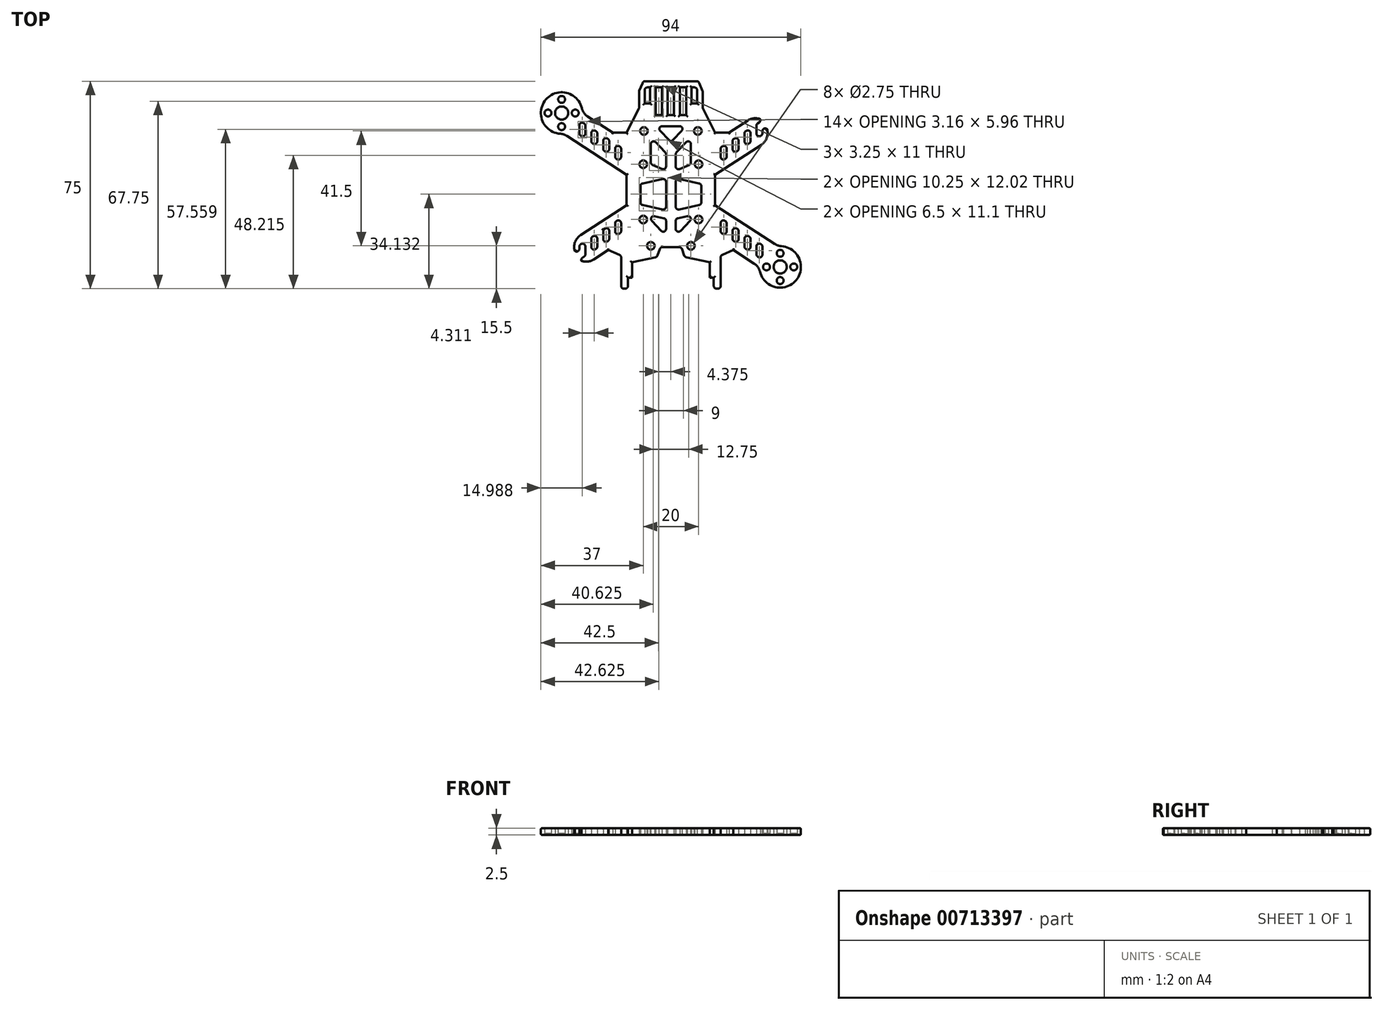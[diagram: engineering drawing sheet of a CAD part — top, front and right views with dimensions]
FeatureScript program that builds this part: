
annotation { "Feature Type Name" : "Feature", "Feature Type Description" : "" }
export const myFeature = defineFeature(function(context is Context, id is Id, definition is map)
    precondition{}
    {
        {
            assignVariable(context, id + "F0", {"name" : "PlateThickness", "anyValue" : 2.5});
        }
        {
            var Q0;
            Q0=qCreatedBy(makeId("Top.planeOp"),FACE);
            var sketch = newSketch(context, id + "F1", { "sketchPlane" : qUnion([Q0])});
            skLineSegment(sketch, "E0.bottom", {"start": v(-10, 35) * mm, "end": v(10, 35) * mm});
            skLineSegment(sketch, "E0.top", {"start": v(-16, -25) * mm, "end": v(16, -25) * mm});
            skLineSegment(sketch, "E0.left", {"start": v(-16, 16.36) * mm, "end": v(-16, -25) * mm});
            skLineSegment(sketch, "E0.right", {"start": v(16, 16.36) * mm, "end": v(16, -25) * mm});
            skPoint(sketch, "E0.middle", {"position": v(0, 5) * mm});
            skLineSegment(sketch, "E1", {"start": v(-10, 35) * mm, "end": v(-11.5, 31.3) * mm});
            skLineSegment(sketch, "E2", {"start": v(-11.5, 31.3) * mm, "end": v(-11.5, 25.3) * mm});
            skLineSegment(sketch, "E3", {"start": v(-11.5, 25.3) * mm, "end": v(-16, 16.36) * mm});
            skPoint(sketch, "E4.orphan", {"position": v(-16, 35) * mm});
            skLineSegment(sketch, "E5", {"start": v(-16, 16.36) * mm, "end": v(-21, 16.36) * mm});
            skLineSegment(sketch, "E6", {"start": v(-21, 16.36) * mm, "end": v(-32, 23.52) * mm});
            skLineSegment(sketch, "E7", {"start": v(-38.83, 16.03) * mm, "end": v(-16, 1.18) * mm});
            skCircle(sketch, "E8", {"center": v(-39.5, 23.5) * mm, "radius": 7.5 * mm});
            skLineSegment(sketch, "E9", {"start": v(0, -4.32) * mm, "end": v(-32.42, -4.32) * mm, "construction": true});
            skLineSegment(sketch, "E10.MirrorCS", {"start": v(-38.83, -24.67) * mm, "end": v(-16, -9.82) * mm});
            skCircle(sketch, "E11.MirrorC", {"center": v(-39.5, -32.14) * mm, "radius": 7.5 * mm});
            skLineSegment(sketch, "E12.MirrorCS", {"start": v(-21, -25) * mm, "end": v(-32, -32.15) * mm});
            skLineSegment(sketch, "E13.MirrorCS", {"start": v(-16, -25) * mm, "end": v(-21, -25) * mm});
            skLineSegment(sketch, "E14.MirrorCS", {"start": v(38.83, 16.03) * mm, "end": v(16, 1.18) * mm});
            skLineSegment(sketch, "E15.MirrorCS", {"start": v(21, 16.36) * mm, "end": v(32, 23.52) * mm});
            skLineSegment(sketch, "E16.MirrorCS", {"start": v(16, 16.36) * mm, "end": v(21, 16.36) * mm});
            skCircle(sketch, "E17.MirrorC", {"center": v(39.5, 23.5) * mm, "radius": 7.5 * mm});
            skLineSegment(sketch, "E18.MirrorCS", {"start": v(38.83, -24.67) * mm, "end": v(16, -9.82) * mm});
            skLineSegment(sketch, "E19.MirrorCS", {"start": v(21, -25) * mm, "end": v(32, -32.15) * mm});
            skLineSegment(sketch, "E20.MirrorCS", {"start": v(16, -25) * mm, "end": v(21, -25) * mm});
            skCircle(sketch, "E21.MirrorC", {"center": v(39.5, -32.14) * mm, "radius": 7.5 * mm});
            skLineSegment(sketch, "E22.MirrorCS", {"start": v(10, 35) * mm, "end": v(11.5, 31.3) * mm});
            skLineSegment(sketch, "E23.MirrorCS", {"start": v(11.5, 31.3) * mm, "end": v(11.5, 25.3) * mm});
            skLineSegment(sketch, "E24.MirrorCS", {"start": v(11.5, 25.3) * mm, "end": v(16, 16.36) * mm});
            skPoint(sketch, "E25.orphan", {"position": v(16, 35) * mm});
            skCircle(sketch, "E26", {"center": v(-39.5, 23.5) * mm, "radius": 2.38 * mm});
            skCircle(sketch, "E27", {"center": v(-39.5, 28.42) * mm, "radius": 1.25 * mm});
            skLineSegment(sketch, "E28", {"start": v(-39.5, 23.5) * mm, "end": v(-47, 23.5) * mm, "construction": true});
            skCircle(sketch, "E29.MirrorC", {"center": v(-39.5, 18.58) * mm, "radius": 1.25 * mm});
            skCircle(sketch, "E30", {"center": v(-44.42, 23.5) * mm, "radius": 1.25 * mm});
            skLineSegment(sketch, "E31", {"start": v(-39.5, 23.5) * mm, "end": v(-39.5, 31) * mm, "construction": true});
            skCircle(sketch, "E32.MirrorC", {"center": v(-34.58, 23.5) * mm, "radius": 1.25 * mm});
            skLineSegment(sketch, "E33", {"start": v(-33.09, 15.63) * mm, "end": v(-18, 5.82) * mm});
            skLineSegment(sketch, "E34", {"start": v(-18, 5.82) * mm, "end": v(-18, 11.07) * mm});
            skLineSegment(sketch, "E35", {"start": v(-18, 11.07) * mm, "end": v(-33.09, 20.88) * mm});
            skLineSegment(sketch, "E36", {"start": v(-33.09, 20.88) * mm, "end": v(-33.09, 15.63) * mm});
            skLineSegment(sketch, "E37", {"start": v(-25.54, 15.98) * mm, "end": v(-25.54, 19.32) * mm, "construction": true});
            skLineSegment(sketch, "E38", {"start": v(-25.54, 10.73) * mm, "end": v(-25.54, 7.39) * mm, "construction": true});
            skLineSegment(sketch, "E39", {"start": v(-30.93, 19.48) * mm, "end": v(-30.93, 14.23) * mm});
            skLineSegment(sketch, "E40", {"start": v(-28.78, 18.08) * mm, "end": v(-28.78, 12.83) * mm});
            skLineSegment(sketch, "E41", {"start": v(-26.62, 16.68) * mm, "end": v(-26.62, 11.43) * mm});
            skLineSegment(sketch, "E42", {"start": v(-24.47, 15.28) * mm, "end": v(-24.47, 10.03) * mm});
            skLineSegment(sketch, "E43", {"start": v(-22.31, 13.87) * mm, "end": v(-22.31, 8.62) * mm});
            skLineSegment(sketch, "E44", {"start": v(-20.16, 12.47) * mm, "end": v(-20.16, 7.22) * mm});
            skLineSegment(sketch, "E45", {"start": v(-33.09, 15.63) * mm, "end": v(-30.93, 14.23) * mm, "construction": true});
            skLineSegment(sketch, "E46", {"start": v(-30.93, 14.23) * mm, "end": v(-28.78, 12.83) * mm, "construction": true});
            skLineSegment(sketch, "E47", {"start": v(-28.78, 12.83) * mm, "end": v(-26.62, 11.43) * mm, "construction": true});
            skLineSegment(sketch, "E48", {"start": v(-26.62, 11.43) * mm, "end": v(-24.47, 10.03) * mm, "construction": true});
            skLineSegment(sketch, "E49", {"start": v(-24.47, 10.03) * mm, "end": v(-22.31, 8.62) * mm, "construction": true});
            skLineSegment(sketch, "E50", {"start": v(-22.31, 8.62) * mm, "end": v(-20.16, 7.22) * mm, "construction": true});
            skLineSegment(sketch, "E51", {"start": v(-20.16, 7.22) * mm, "end": v(-18, 5.82) * mm, "construction": true});
            skLineSegment(sketch, "E52.MirrorCS", {"start": v(33.09, 15.63) * mm, "end": v(18, 5.82) * mm});
            skLineSegment(sketch, "E53.MirrorCS", {"start": v(26.62, 11.43) * mm, "end": v(24.47, 10.03) * mm, "construction": true});
            skLineSegment(sketch, "E54.MirrorCS", {"start": v(30.93, 14.23) * mm, "end": v(28.78, 12.83) * mm, "construction": true});
            skLineSegment(sketch, "E55.MirrorCS", {"start": v(25.54, 15.98) * mm, "end": v(25.54, 19.32) * mm, "construction": true});
            skLineSegment(sketch, "E56.MirrorCS", {"start": v(33.09, 15.63) * mm, "end": v(30.93, 14.23) * mm, "construction": true});
            skLineSegment(sketch, "E57.MirrorCS", {"start": v(22.31, 8.62) * mm, "end": v(20.16, 7.22) * mm, "construction": true});
            skLineSegment(sketch, "E58.MirrorCS", {"start": v(28.78, 18.08) * mm, "end": v(28.78, 12.83) * mm});
            skLineSegment(sketch, "E59.MirrorCS", {"start": v(30.93, 19.48) * mm, "end": v(30.93, 14.23) * mm});
            skLineSegment(sketch, "E60.MirrorCS", {"start": v(24.47, 15.28) * mm, "end": v(24.47, 10.03) * mm});
            skLineSegment(sketch, "E61.MirrorCS", {"start": v(18, 11.07) * mm, "end": v(33.09, 20.88) * mm});
            skLineSegment(sketch, "E62.MirrorCS", {"start": v(24.47, 10.03) * mm, "end": v(22.31, 8.62) * mm, "construction": true});
            skLineSegment(sketch, "E63.MirrorCS", {"start": v(28.78, 12.83) * mm, "end": v(26.62, 11.43) * mm, "construction": true});
            skLineSegment(sketch, "E64.MirrorCS", {"start": v(26.62, 16.68) * mm, "end": v(26.62, 11.43) * mm});
            skLineSegment(sketch, "E65.MirrorCS", {"start": v(20.16, 12.47) * mm, "end": v(20.16, 7.22) * mm});
            skLineSegment(sketch, "E66.MirrorCS", {"start": v(33.09, 20.88) * mm, "end": v(33.09, 15.63) * mm});
            skLineSegment(sketch, "E67.MirrorCS", {"start": v(25.54, 10.73) * mm, "end": v(25.54, 7.39) * mm, "construction": true});
            skLineSegment(sketch, "E68.MirrorCS", {"start": v(18, 5.82) * mm, "end": v(18, 11.07) * mm});
            skLineSegment(sketch, "E69.MirrorCS", {"start": v(20.16, 7.22) * mm, "end": v(18, 5.82) * mm, "construction": true});
            skLineSegment(sketch, "E70.MirrorCS", {"start": v(22.31, 13.87) * mm, "end": v(22.31, 8.62) * mm});
            skCircle(sketch, "E71.MirrorC", {"center": v(39.5, 18.58) * mm, "radius": 1.25 * mm});
            skCircle(sketch, "E72.MirrorC", {"center": v(34.58, 23.5) * mm, "radius": 1.25 * mm});
            skCircle(sketch, "E73.MirrorC", {"center": v(39.5, 23.5) * mm, "radius": 2.38 * mm});
            skCircle(sketch, "E74.MirrorC", {"center": v(39.5, 28.43) * mm, "radius": 1.25 * mm});
            skCircle(sketch, "E75.MirrorC", {"center": v(44.42, 23.5) * mm, "radius": 1.25 * mm});
            skLineSegment(sketch, "E76.MirrorCS", {"start": v(33.09, -24.27) * mm, "end": v(18, -14.46) * mm});
            skLineSegment(sketch, "E77.MirrorCS", {"start": v(30.93, -22.87) * mm, "end": v(28.78, -21.47) * mm, "construction": true});
            skLineSegment(sketch, "E78.MirrorCS", {"start": v(28.78, -21.47) * mm, "end": v(26.62, -20.07) * mm, "construction": true});
            skLineSegment(sketch, "E79.MirrorCS", {"start": v(24.47, -18.67) * mm, "end": v(22.31, -17.26) * mm, "construction": true});
            skLineSegment(sketch, "E80.MirrorCS", {"start": v(22.31, -17.26) * mm, "end": v(20.16, -15.86) * mm, "construction": true});
            skLineSegment(sketch, "E81.MirrorCS", {"start": v(20.16, -15.86) * mm, "end": v(18, -14.46) * mm, "construction": true});
            skLineSegment(sketch, "E82.MirrorCS", {"start": v(26.62, -20.07) * mm, "end": v(24.47, -18.67) * mm, "construction": true});
            skLineSegment(sketch, "E83.MirrorCS", {"start": v(33.09, -24.27) * mm, "end": v(30.93, -22.87) * mm, "construction": true});
            skLineSegment(sketch, "E84.MirrorCS", {"start": v(24.47, -23.92) * mm, "end": v(24.47, -18.67) * mm});
            skLineSegment(sketch, "E85.MirrorCS", {"start": v(18, -14.46) * mm, "end": v(18, -19.7) * mm});
            skLineSegment(sketch, "E86.MirrorCS", {"start": v(25.54, -19.37) * mm, "end": v(25.54, -16.03) * mm, "construction": true});
            skLineSegment(sketch, "E87.MirrorCS", {"start": v(22.31, -22.51) * mm, "end": v(22.31, -17.26) * mm});
            skLineSegment(sketch, "E88.MirrorCS", {"start": v(28.78, -26.72) * mm, "end": v(28.78, -21.47) * mm});
            skLineSegment(sketch, "E89.MirrorCS", {"start": v(30.93, -28.12) * mm, "end": v(30.93, -22.87) * mm});
            skLineSegment(sketch, "E90.MirrorCS", {"start": v(25.54, -24.62) * mm, "end": v(25.54, -27.96) * mm, "construction": true});
            skLineSegment(sketch, "E91.MirrorCS", {"start": v(26.62, -25.32) * mm, "end": v(26.62, -20.07) * mm});
            skLineSegment(sketch, "E92.MirrorCS", {"start": v(20.16, -21.11) * mm, "end": v(20.16, -15.86) * mm});
            skLineSegment(sketch, "E93.MirrorCS", {"start": v(18, -19.7) * mm, "end": v(33.09, -29.52) * mm});
            skLineSegment(sketch, "E94.MirrorCS", {"start": v(33.09, -29.52) * mm, "end": v(33.09, -24.27) * mm});
            skCircle(sketch, "E95.MirrorC", {"center": v(39.5, -27.21) * mm, "radius": 1.25 * mm});
            skCircle(sketch, "E96.MirrorC", {"center": v(39.5, -32.14) * mm, "radius": 2.38 * mm});
            skCircle(sketch, "E97.MirrorC", {"center": v(34.58, -32.14) * mm, "radius": 1.25 * mm});
            skCircle(sketch, "E98.MirrorC", {"center": v(39.5, -37.06) * mm, "radius": 1.25 * mm});
            skCircle(sketch, "E99.MirrorC", {"center": v(44.42, -32.14) * mm, "radius": 1.25 * mm});
            skLineSegment(sketch, "E100.MirrorCS", {"start": v(-28.78, -21.47) * mm, "end": v(-26.62, -20.07) * mm, "construction": true});
            skLineSegment(sketch, "E101.MirrorCS", {"start": v(-33.09, -24.27) * mm, "end": v(-18, -14.46) * mm});
            skLineSegment(sketch, "E102.MirrorCS", {"start": v(-26.62, -20.07) * mm, "end": v(-24.47, -18.67) * mm, "construction": true});
            skLineSegment(sketch, "E103.MirrorCS", {"start": v(-25.54, -19.37) * mm, "end": v(-25.54, -16.03) * mm, "construction": true});
            skLineSegment(sketch, "E104.MirrorCS", {"start": v(-26.62, -25.32) * mm, "end": v(-26.62, -20.07) * mm});
            skLineSegment(sketch, "E105.MirrorCS", {"start": v(-24.47, -23.92) * mm, "end": v(-24.47, -18.67) * mm});
            skLineSegment(sketch, "E106.MirrorCS", {"start": v(-24.47, -18.67) * mm, "end": v(-22.31, -17.26) * mm, "construction": true});
            skLineSegment(sketch, "E107.MirrorCS", {"start": v(-28.78, -26.72) * mm, "end": v(-28.78, -21.47) * mm});
            skLineSegment(sketch, "E108.MirrorCS", {"start": v(-33.09, -24.27) * mm, "end": v(-30.93, -22.87) * mm, "construction": true});
            skLineSegment(sketch, "E109.MirrorCS", {"start": v(-22.31, -17.26) * mm, "end": v(-20.16, -15.86) * mm, "construction": true});
            skLineSegment(sketch, "E110.MirrorCS", {"start": v(-22.31, -22.51) * mm, "end": v(-22.31, -17.26) * mm});
            skLineSegment(sketch, "E111.MirrorCS", {"start": v(-30.93, -22.87) * mm, "end": v(-28.78, -21.47) * mm, "construction": true});
            skLineSegment(sketch, "E112.MirrorCS", {"start": v(-20.16, -15.86) * mm, "end": v(-18, -14.46) * mm, "construction": true});
            skLineSegment(sketch, "E113.MirrorCS", {"start": v(-20.16, -21.11) * mm, "end": v(-20.16, -15.86) * mm});
            skLineSegment(sketch, "E114.MirrorCS", {"start": v(-33.09, -29.52) * mm, "end": v(-33.09, -24.27) * mm});
            skLineSegment(sketch, "E115.MirrorCS", {"start": v(-25.54, -24.62) * mm, "end": v(-25.54, -27.96) * mm, "construction": true});
            skLineSegment(sketch, "E116.MirrorCS", {"start": v(-18, -14.46) * mm, "end": v(-18, -19.7) * mm});
            skLineSegment(sketch, "E117.MirrorCS", {"start": v(-30.93, -28.12) * mm, "end": v(-30.93, -22.87) * mm});
            skLineSegment(sketch, "E118.MirrorCS", {"start": v(-18, -19.7) * mm, "end": v(-33.09, -29.52) * mm});
            skCircle(sketch, "E119.MirrorC", {"center": v(-39.5, -27.21) * mm, "radius": 1.25 * mm});
            skCircle(sketch, "E120.MirrorC", {"center": v(-34.58, -32.14) * mm, "radius": 1.25 * mm});
            skCircle(sketch, "E121.MirrorC", {"center": v(-44.42, -32.14) * mm, "radius": 1.25 * mm});
            skCircle(sketch, "E122.MirrorC", {"center": v(-39.5, -37.06) * mm, "radius": 1.25 * mm});
            skCircle(sketch, "E123.MirrorC", {"center": v(-39.5, -32.14) * mm, "radius": 2.38 * mm});
            skLineSegment(sketch, "E124.bottom", {"start": v(-7.5, 27) * mm, "end": v(-9.5, 27) * mm});
            skLineSegment(sketch, "E124.top", {"start": v(-7.5, 32.75) * mm, "end": v(-9.5, 32.75) * mm});
            skLineSegment(sketch, "E124.left", {"start": v(-7.5, 27) * mm, "end": v(-7.5, 32.75) * mm});
            skLineSegment(sketch, "E124.right", {"start": v(-9.5, 27) * mm, "end": v(-9.5, 32.75) * mm});
            skPoint(sketch, "E124.middle", {"position": v(-8.5, 29.88) * mm});
            skLineSegment(sketch, "E125.MirrorCS", {"start": v(7.5, 27) * mm, "end": v(9.5, 27) * mm});
            skLineSegment(sketch, "E126.MirrorCS", {"start": v(7.5, 27) * mm, "end": v(7.5, 32.75) * mm});
            skLineSegment(sketch, "E127.MirrorCS", {"start": v(9.5, 27) * mm, "end": v(9.5, 32.75) * mm});
            skLineSegment(sketch, "E128.MirrorCS", {"start": v(7.5, 32.75) * mm, "end": v(9.5, 32.75) * mm});
            skLineSegment(sketch, "E129.bottom", {"start": v(-5.5, 32.75) * mm, "end": v(-3.25, 32.75) * mm});
            skLineSegment(sketch, "E129.top", {"start": v(-5.5, 22.75) * mm, "end": v(-3.25, 22.75) * mm});
            skLineSegment(sketch, "E129.left", {"start": v(-5.5, 32.75) * mm, "end": v(-5.5, 22.75) * mm});
            skLineSegment(sketch, "E129.right", {"start": v(-3.25, 32.75) * mm, "end": v(-3.25, 22.75) * mm});
            skPoint(sketch, "E129.middle", {"position": v(-4.37, 27.75) * mm});
            skLineSegment(sketch, "E130.MirrorCS", {"start": v(3.25, 32.75) * mm, "end": v(3.25, 22.75) * mm});
            skLineSegment(sketch, "E131.MirrorCS", {"start": v(5.5, 32.75) * mm, "end": v(3.25, 32.75) * mm});
            skLineSegment(sketch, "E132.MirrorCS", {"start": v(5.5, 32.75) * mm, "end": v(5.5, 22.75) * mm});
            skLineSegment(sketch, "E133.MirrorCS", {"start": v(5.5, 22.75) * mm, "end": v(3.25, 22.75) * mm});
            skLineSegment(sketch, "E134.bottom", {"start": v(-1.13, 32.75) * mm, "end": v(1.12, 32.75) * mm});
            skLineSegment(sketch, "E134.top", {"start": v(-1.13, 22.75) * mm, "end": v(1.12, 22.75) * mm});
            skLineSegment(sketch, "E134.left", {"start": v(-1.13, 32.75) * mm, "end": v(-1.13, 22.75) * mm});
            skLineSegment(sketch, "E134.right", {"start": v(1.12, 32.75) * mm, "end": v(1.13, 22.75) * mm});
            skPoint(sketch, "E134.middle", {"position": v(0, 27.75) * mm});
            skLineSegment(sketch, "E135", {"start": v(-5.5, 18.75) * mm, "end": v(5.5, 18.75) * mm});
            skLineSegment(sketch, "E136", {"start": v(5.5, 18.75) * mm, "end": v(0, 12.94) * mm});
            skLineSegment(sketch, "E137", {"start": v(0, 12.94) * mm, "end": v(-5.5, 18.75) * mm});
            skLineSegment(sketch, "E138", {"start": v(-7.25, 14.78) * mm, "end": v(-1.75, 8.97) * mm});
            skLineSegment(sketch, "E139", {"start": v(-1.75, 8.97) * mm, "end": v(-1.75, 2.63) * mm});
            skLineSegment(sketch, "E140", {"start": v(-1.75, 2.63) * mm, "end": v(-7.25, 5.03) * mm});
            skLineSegment(sketch, "E141", {"start": v(-7.25, 5.03) * mm, "end": v(-7.25, 14.78) * mm});
            skLineSegment(sketch, "E142.MirrorCS", {"start": v(1.75, 8.97) * mm, "end": v(1.75, 2.63) * mm});
            skLineSegment(sketch, "E143.MirrorCS", {"start": v(7.25, 14.78) * mm, "end": v(1.75, 8.97) * mm});
            skLineSegment(sketch, "E144.MirrorCS", {"start": v(7.25, 5.03) * mm, "end": v(7.25, 14.78) * mm});
            skLineSegment(sketch, "E145.MirrorCS", {"start": v(1.75, 2.63) * mm, "end": v(7.25, 5.03) * mm});
            skLineSegment(sketch, "E146", {"start": v(-11, -2.12) * mm, "end": v(-11, -9.62) * mm});
            skLineSegment(sketch, "E147", {"start": v(-11, -9.62) * mm, "end": v(-1.75, -11.62) * mm});
            skLineSegment(sketch, "E148", {"start": v(-1.75, -11.62) * mm, "end": v(-1.75, -0.12) * mm});
            skLineSegment(sketch, "E149", {"start": v(-1.75, -0.12) * mm, "end": v(-11, -2.12) * mm});
            skLineSegment(sketch, "E150.MirrorCS", {"start": v(1.75, -0.12) * mm, "end": v(11, -2.12) * mm});
            skLineSegment(sketch, "E151.MirrorCS", {"start": v(1.75, -11.62) * mm, "end": v(1.75, -0.12) * mm});
            skLineSegment(sketch, "E152.MirrorCS", {"start": v(11, -2.12) * mm, "end": v(11, -9.62) * mm});
            skLineSegment(sketch, "E153.MirrorCS", {"start": v(11, -9.62) * mm, "end": v(1.75, -11.62) * mm});
            skLineSegment(sketch, "E154", {"start": v(-9.1, -13.1) * mm, "end": v(-1.75, -14.69) * mm});
            skLineSegment(sketch, "E155", {"start": v(-1.75, -14.69) * mm, "end": v(-1.75, -20.94) * mm});
            skLineSegment(sketch, "E156", {"start": v(-1.75, -20.94) * mm, "end": v(-9.1, -13.1) * mm});
            skLineSegment(sketch, "E157.MirrorCS", {"start": v(9.1, -13.1) * mm, "end": v(1.75, -14.69) * mm});
            skLineSegment(sketch, "E158.MirrorCS", {"start": v(1.75, -14.69) * mm, "end": v(1.75, -20.94) * mm});
            skLineSegment(sketch, "E159.MirrorCS", {"start": v(1.75, -20.94) * mm, "end": v(9.1, -13.1) * mm});
            skLineSegment(sketch, "E160", {"start": v(-3.75, -25) * mm, "end": v(-5, -28.5) * mm});
            skLineSegment(sketch, "E161", {"start": v(-5, -28.5) * mm, "end": v(-14, -30.5) * mm});
            skLineSegment(sketch, "E162", {"start": v(-14, -30.5) * mm, "end": v(-14, -36) * mm});
            skLineSegment(sketch, "E163", {"start": v(-14, -36) * mm, "end": v(-15.5, -36) * mm});
            skLineSegment(sketch, "E164", {"start": v(-15.5, -36) * mm, "end": v(-15.5, -40) * mm});
            skLineSegment(sketch, "E165", {"start": v(-15.5, -40) * mm, "end": v(-18, -40) * mm});
            skLineSegment(sketch, "E166", {"start": v(-18, -40) * mm, "end": v(-18, -28) * mm});
            skLineSegment(sketch, "E167", {"start": v(-18, -28) * mm, "end": v(-22.6, -26.04) * mm});
            skLineSegment(sketch, "E168.MirrorCS", {"start": v(3.75, -25) * mm, "end": v(5, -28.5) * mm});
            skLineSegment(sketch, "E169.MirrorCS", {"start": v(5, -28.5) * mm, "end": v(14, -30.5) * mm});
            skLineSegment(sketch, "E170.MirrorCS", {"start": v(14, -30.5) * mm, "end": v(14, -36) * mm});
            skLineSegment(sketch, "E171.MirrorCS", {"start": v(15.5, -36) * mm, "end": v(15.5, -40) * mm});
            skLineSegment(sketch, "E172.MirrorCS", {"start": v(15.5, -40) * mm, "end": v(18, -40) * mm});
            skLineSegment(sketch, "E173.MirrorCS", {"start": v(18, -40) * mm, "end": v(18, -28) * mm});
            skLineSegment(sketch, "E174.MirrorCS", {"start": v(18, -28) * mm, "end": v(22.6, -26.04) * mm});
            skLineSegment(sketch, "E175.MirrorCS", {"start": v(14, -36) * mm, "end": v(15.5, -36) * mm});
            skCircle(sketch, "E176", {"center": v(-9.75, 17) * mm, "radius": 1.38 * mm});
            skCircle(sketch, "E177.MirrorC", {"center": v(9.75, 17) * mm, "radius": 1.38 * mm});
            skCircle(sketch, "E178", {"center": v(-7.25, -24.5) * mm, "radius": 1.38 * mm});
            skCircle(sketch, "E179.MirrorC", {"center": v(7.25, -24.5) * mm, "radius": 1.38 * mm});
            skCircle(sketch, "E180", {"center": v(10, 5) * mm, "radius": 1.38 * mm});
            skCircle(sketch, "E181", {"center": v(10, -15) * mm, "radius": 1.38 * mm});
            skCircle(sketch, "E182", {"center": v(-10, -15) * mm, "radius": 1.38 * mm});
            skCircle(sketch, "E183", {"center": v(-10, 5) * mm, "radius": 1.38 * mm});
            skPoint(sketch, "E184", {"position": v(-39.5, 0) * mm});
            skSolve(sketch);
        }
        {
            var Q0;
            Q0=makeQuery(id+"F1.imprint","IMPRINT",FACE,{"disambiguationData":[TD([[makeQuery(id+"F1.imprint","IMPRINT",EDGE,{"derivedFrom":sQuery(id+"F1.wireOp",EDGE,"E0.bottom")}),-1.0]])]});
            var Q1;
            {var subQ15=sQuery(id+"F1.wireOp",EDGE,"E5");Q1=makeQuery(id+"F1.imprint","IMPRINT",FACE,{"disambiguationData":[TD([[makeQuery(id+"F1.imprint","IMPRINT",EDGE,{"derivedFrom":subQ15}),1.0]])]});}
            var Q2;
            Q2=makeQuery(id+"F1.imprint","IMPRINT",FACE,{"disambiguationData":[TD([[makeQuery(id+"F1.imprint","IMPRINT",EDGE,{"derivedFrom":sQuery(id+"F1.wireOp",EDGE,"E26")}),-1.0]])]});
            var Q3;
            {var subQ2=sQuery(id+"F1.wireOp",EDGE,"E14.MirrorCS");Q3=makeQuery(id+"F1.imprint","IMPRINT",FACE,{"disambiguationData":[TD([[makeQuery(id+"F1.imprint","IMPRINT",EDGE,{"derivedFrom":subQ2}),-1.0]])]});}
            var Q4;
            {var subQ0=sQuery(id+"F1.wireOp",EDGE,"E17.MirrorC");var subQ1=makeQuery(id+"F1.imprint","INTERSECT",VERTEX,{"derivedFrom":[sQuery(id+"F1.wireOp",EDGE,"E14.MirrorCS"),subQ0]});Q4=makeQuery(id+"F1.imprint","IMPRINT",FACE,{"disambiguationData":[TD([[makeQuery(id+"F1.imprint","IMPRINT",EDGE,{"disambiguationData":[TD([[subQ1,1.0]])],"derivedFrom":subQ0}),-1.0]])]});}
            var Q5;
            {var subQ1=sQuery(id+"F1.wireOp",EDGE,"E18.MirrorCS");Q5=makeQuery(id+"F1.imprint","IMPRINT",FACE,{"disambiguationData":[TD([[makeQuery(id+"F1.imprint","IMPRINT",EDGE,{"derivedFrom":subQ1}),1.0]])]});}
            var Q6;
            {var subQ2=sQuery(id+"F1.wireOp",EDGE,"E10.MirrorCS");Q6=makeQuery(id+"F1.imprint","IMPRINT",FACE,{"disambiguationData":[TD([[makeQuery(id+"F1.imprint","IMPRINT",EDGE,{"derivedFrom":subQ2}),-1.0]])]});}
            var Q7;
            {var subQ0=sQuery(id+"F1.wireOp",EDGE,"E21.MirrorC");var subQ1=makeQuery(id+"F1.imprint","INTERSECT",VERTEX,{"derivedFrom":[sQuery(id+"F1.wireOp",EDGE,"E18.MirrorCS"),subQ0]});Q7=makeQuery(id+"F1.imprint","IMPRINT",FACE,{"disambiguationData":[TD([[makeQuery(id+"F1.imprint","IMPRINT",EDGE,{"disambiguationData":[TD([[subQ1,1.0]])],"derivedFrom":subQ0}),1.0]])]});}
            var Q8;
            {var subQ0=sQuery(id+"F1.wireOp",EDGE,"E39");Q8=makeQuery(id+"F1.imprint","IMPRINT",FACE,{"disambiguationData":[TD([[makeQuery(id+"F1.imprint","IMPRINT",EDGE,{"derivedFrom":subQ0}),1.0]])]});}
            var Q9;
            {var subQ0=sQuery(id+"F1.wireOp",EDGE,"E41");Q9=makeQuery(id+"F1.imprint","IMPRINT",FACE,{"disambiguationData":[TD([[makeQuery(id+"F1.imprint","IMPRINT",EDGE,{"derivedFrom":subQ0}),1.0]])]});}
            var Q10;
            {var subQ0=sQuery(id+"F1.wireOp",EDGE,"E43");Q10=makeQuery(id+"F1.imprint","IMPRINT",FACE,{"disambiguationData":[TD([[makeQuery(id+"F1.imprint","IMPRINT",EDGE,{"derivedFrom":subQ0}),1.0]])]});}
            var Q11;
            {var subQ0=sQuery(id+"F1.wireOp",EDGE,"E11.MirrorC");var subQ1=makeQuery(id+"F1.imprint","INTERSECT",VERTEX,{"derivedFrom":[sQuery(id+"F1.wireOp",EDGE,"E10.MirrorCS"),subQ0]});Q11=makeQuery(id+"F1.imprint","IMPRINT",FACE,{"disambiguationData":[TD([[makeQuery(id+"F1.imprint","IMPRINT",EDGE,{"disambiguationData":[TD([[subQ1,1.0]])],"derivedFrom":subQ0}),-1.0]])]});}
            var Q12;
            {var subQ15=sQuery(id+"F1.wireOp",EDGE,"E12.MirrorCS");Q12=makeQuery(id+"F1.imprint","IMPRINT",FACE,{"disambiguationData":[TD([[makeQuery(id+"F1.imprint","IMPRINT",EDGE,{"derivedFrom":subQ15}),-1.0]])]});}
            var Q13;
            {var subQ0=sQuery(id+"F1.wireOp",EDGE,"E58.MirrorCS");Q13=makeQuery(id+"F1.imprint","IMPRINT",FACE,{"disambiguationData":[TD([[makeQuery(id+"F1.imprint","IMPRINT",EDGE,{"derivedFrom":subQ0}),1.0]])]});}
            var Q14;
            {var subQ0=sQuery(id+"F1.wireOp",EDGE,"E60.MirrorCS");Q14=makeQuery(id+"F1.imprint","IMPRINT",FACE,{"disambiguationData":[TD([[makeQuery(id+"F1.imprint","IMPRINT",EDGE,{"derivedFrom":subQ0}),1.0]])]});}
            var Q15;
            {var subQ0=sQuery(id+"F1.wireOp",EDGE,"E65.MirrorCS");Q15=makeQuery(id+"F1.imprint","IMPRINT",FACE,{"disambiguationData":[TD([[makeQuery(id+"F1.imprint","IMPRINT",EDGE,{"derivedFrom":subQ0}),1.0]])]});}
            var Q16;
            {var subQ0=sQuery(id+"F1.wireOp",EDGE,"E107.MirrorCS");Q16=makeQuery(id+"F1.imprint","IMPRINT",FACE,{"disambiguationData":[TD([[makeQuery(id+"F1.imprint","IMPRINT",EDGE,{"derivedFrom":subQ0}),1.0]])]});}
            var Q17;
            {var subQ0=sQuery(id+"F1.wireOp",EDGE,"E104.MirrorCS");Q17=makeQuery(id+"F1.imprint","IMPRINT",FACE,{"disambiguationData":[TD([[makeQuery(id+"F1.imprint","IMPRINT",EDGE,{"derivedFrom":subQ0}),-1.0]])]});}
            var Q18;
            {var subQ0=sQuery(id+"F1.wireOp",EDGE,"E110.MirrorCS");Q18=makeQuery(id+"F1.imprint","IMPRINT",FACE,{"disambiguationData":[TD([[makeQuery(id+"F1.imprint","IMPRINT",EDGE,{"derivedFrom":subQ0}),-1.0]])]});}
            var Q19;
            {var subQ0=sQuery(id+"F1.wireOp",EDGE,"E88.MirrorCS");Q19=makeQuery(id+"F1.imprint","IMPRINT",FACE,{"disambiguationData":[TD([[makeQuery(id+"F1.imprint","IMPRINT",EDGE,{"derivedFrom":subQ0}),-1.0]])]});}
            var Q20;
            {var subQ0=sQuery(id+"F1.wireOp",EDGE,"E84.MirrorCS");Q20=makeQuery(id+"F1.imprint","IMPRINT",FACE,{"disambiguationData":[TD([[makeQuery(id+"F1.imprint","IMPRINT",EDGE,{"derivedFrom":subQ0}),-1.0]])]});}
            var Q21;
            {var subQ0=sQuery(id+"F1.wireOp",EDGE,"E87.MirrorCS");Q21=makeQuery(id+"F1.imprint","IMPRINT",FACE,{"disambiguationData":[TD([[makeQuery(id+"F1.imprint","IMPRINT",EDGE,{"derivedFrom":subQ0}),1.0]])]});}
            var Q22;
            {var subQ0=sQuery(id+"F1.wireOp",EDGE,"E13.MirrorCS");Q22=makeQuery(id+"F1.imprint","IMPRINT",FACE,{"disambiguationData":[TD([[makeQuery(id+"F1.imprint","IMPRINT",EDGE,{"derivedFrom":subQ0}),1.0]])]});}
            var Q23;
            {var subQ1=sQuery(id+"F1.wireOp",EDGE,"E20.MirrorCS");Q23=makeQuery(id+"F1.imprint","IMPRINT",FACE,{"disambiguationData":[TD([[makeQuery(id+"F1.imprint","IMPRINT",EDGE,{"derivedFrom":subQ1}),-1.0]])]});}
            extrude(context, id + "F2", {"entities" : qUnion([Q0, Q1, Q2, Q3, Q4, Q5, Q6, Q7, Q8, Q9, Q10, Q11, Q12, Q13, Q14, Q15, Q16, Q17, Q18, Q19, Q20, Q21, Q22, Q23]), "depth" : (getVariable(context, 'PlateThickness')) * mm, "offsetDistance" : 25 * mm});
        }
        {
            var Q0;
            Q0=makeQuery(id+"F2.opExtrude","SWEPT_EDGE",EDGE,{"disambiguationData":[OSD([sQuery(id+"F1.wireOp",EDGE,"E35"),sQuery(id+"F1.wireOp",EDGE,"E36")])]});
            var Q1;
            Q1=makeQuery(id+"F2.opExtrude","SWEPT_EDGE",EDGE,{"disambiguationData":[OSD([sQuery(id+"F1.wireOp",EDGE,"E35"),sQuery(id+"F1.wireOp",EDGE,"E39")])]});
            var Q2;
            Q2=makeQuery(id+"F2.opExtrude","SWEPT_EDGE",EDGE,{"disambiguationData":[OSD([sQuery(id+"F1.wireOp",EDGE,"E33"),sQuery(id+"F1.wireOp",EDGE,"E36")])]});
            var Q3;
            Q3=makeQuery(id+"F2.opExtrude","SWEPT_EDGE",EDGE,{"disambiguationData":[OSD([sQuery(id+"F1.wireOp",EDGE,"E33"),sQuery(id+"F1.wireOp",EDGE,"E39")])]});
            var Q4;
            Q4=makeQuery(id+"F2.opExtrude","SWEPT_EDGE",EDGE,{"disambiguationData":[OSD([sQuery(id+"F1.wireOp",EDGE,"E33"),sQuery(id+"F1.wireOp",EDGE,"E41")])]});
            var Q5;
            Q5=makeQuery(id+"F2.opExtrude","SWEPT_EDGE",EDGE,{"disambiguationData":[OSD([sQuery(id+"F1.wireOp",EDGE,"E35"),sQuery(id+"F1.wireOp",EDGE,"E41")])]});
            var Q6;
            Q6=makeQuery(id+"F2.opExtrude","SWEPT_EDGE",EDGE,{"disambiguationData":[OSD([sQuery(id+"F1.wireOp",EDGE,"E35"),sQuery(id+"F1.wireOp",EDGE,"E40")])]});
            var Q7;
            Q7=makeQuery(id+"F2.opExtrude","SWEPT_EDGE",EDGE,{"disambiguationData":[OSD([sQuery(id+"F1.wireOp",EDGE,"E33"),sQuery(id+"F1.wireOp",EDGE,"E40")])]});
            var Q8;
            Q8=makeQuery(id+"F2.opExtrude","SWEPT_EDGE",EDGE,{"disambiguationData":[OSD([sQuery(id+"F1.wireOp",EDGE,"E33"),sQuery(id+"F1.wireOp",EDGE,"E42")])]});
            var Q9;
            Q9=makeQuery(id+"F2.opExtrude","SWEPT_EDGE",EDGE,{"disambiguationData":[OSD([sQuery(id+"F1.wireOp",EDGE,"E33"),sQuery(id+"F1.wireOp",EDGE,"E43")])]});
            var Q10;
            Q10=makeQuery(id+"F2.opExtrude","SWEPT_EDGE",EDGE,{"disambiguationData":[OSD([sQuery(id+"F1.wireOp",EDGE,"E35"),sQuery(id+"F1.wireOp",EDGE,"E43")])]});
            var Q11;
            Q11=makeQuery(id+"F2.opExtrude","SWEPT_EDGE",EDGE,{"disambiguationData":[OSD([sQuery(id+"F1.wireOp",EDGE,"E35"),sQuery(id+"F1.wireOp",EDGE,"E42")])]});
            var Q12;
            Q12=makeQuery(id+"F2.opExtrude","SWEPT_EDGE",EDGE,{"disambiguationData":[OSD([sQuery(id+"F1.wireOp",EDGE,"E33"),sQuery(id+"F1.wireOp",EDGE,"E34")])]});
            var Q13;
            Q13=makeQuery(id+"F2.opExtrude","SWEPT_EDGE",EDGE,{"disambiguationData":[OSD([sQuery(id+"F1.wireOp",EDGE,"E34"),sQuery(id+"F1.wireOp",EDGE,"E35")])]});
            var Q14;
            Q14=makeQuery(id+"F2.opExtrude","SWEPT_EDGE",EDGE,{"disambiguationData":[OSD([sQuery(id+"F1.wireOp",EDGE,"E35"),sQuery(id+"F1.wireOp",EDGE,"E44")])]});
            var Q15;
            Q15=makeQuery(id+"F2.opExtrude","SWEPT_EDGE",EDGE,{"disambiguationData":[OSD([sQuery(id+"F1.wireOp",EDGE,"E33"),sQuery(id+"F1.wireOp",EDGE,"E44")])]});
            var Q16;
            Q16=makeQuery(id+"F2.opExtrude","SWEPT_EDGE",EDGE,{"disambiguationData":[OSD([sQuery(id+"F1.wireOp",EDGE,"E52.MirrorCS"),sQuery(id+"F1.wireOp",EDGE,"E68.MirrorCS")])]});
            var Q17;
            Q17=makeQuery(id+"F2.opExtrude","SWEPT_EDGE",EDGE,{"disambiguationData":[OSD([sQuery(id+"F1.wireOp",EDGE,"E52.MirrorCS"),sQuery(id+"F1.wireOp",EDGE,"E65.MirrorCS")])]});
            var Q18;
            Q18=makeQuery(id+"F2.opExtrude","SWEPT_EDGE",EDGE,{"disambiguationData":[OSD([sQuery(id+"F1.wireOp",EDGE,"E61.MirrorCS"),sQuery(id+"F1.wireOp",EDGE,"E65.MirrorCS")])]});
            var Q19;
            Q19=makeQuery(id+"F2.opExtrude","SWEPT_EDGE",EDGE,{"disambiguationData":[OSD([sQuery(id+"F1.wireOp",EDGE,"E61.MirrorCS"),sQuery(id+"F1.wireOp",EDGE,"E68.MirrorCS")])]});
            var Q20;
            Q20=makeQuery(id+"F2.opExtrude","SWEPT_EDGE",EDGE,{"disambiguationData":[OSD([sQuery(id+"F1.wireOp",EDGE,"E61.MirrorCS"),sQuery(id+"F1.wireOp",EDGE,"E70.MirrorCS")])]});
            var Q21;
            Q21=makeQuery(id+"F2.opExtrude","SWEPT_EDGE",EDGE,{"disambiguationData":[OSD([sQuery(id+"F1.wireOp",EDGE,"E61.MirrorCS"),sQuery(id+"F1.wireOp",EDGE,"E64.MirrorCS")])]});
            var Q22;
            Q22=makeQuery(id+"F2.opExtrude","SWEPT_EDGE",EDGE,{"disambiguationData":[OSD([sQuery(id+"F1.wireOp",EDGE,"E59.MirrorCS"),sQuery(id+"F1.wireOp",EDGE,"E61.MirrorCS")])]});
            var Q23;
            Q23=makeQuery(id+"F2.opExtrude","SWEPT_EDGE",EDGE,{"disambiguationData":[OSD([sQuery(id+"F1.wireOp",EDGE,"E60.MirrorCS"),sQuery(id+"F1.wireOp",EDGE,"E61.MirrorCS")])]});
            var Q24;
            Q24=makeQuery(id+"F2.opExtrude","SWEPT_EDGE",EDGE,{"disambiguationData":[OSD([sQuery(id+"F1.wireOp",EDGE,"E58.MirrorCS"),sQuery(id+"F1.wireOp",EDGE,"E61.MirrorCS")])]});
            var Q25;
            Q25=makeQuery(id+"F2.opExtrude","SWEPT_EDGE",EDGE,{"disambiguationData":[OSD([sQuery(id+"F1.wireOp",EDGE,"E61.MirrorCS"),sQuery(id+"F1.wireOp",EDGE,"E66.MirrorCS")])]});
            var Q26;
            Q26=makeQuery(id+"F2.opExtrude","SWEPT_EDGE",EDGE,{"disambiguationData":[OSD([sQuery(id+"F1.wireOp",EDGE,"E52.MirrorCS"),sQuery(id+"F1.wireOp",EDGE,"E66.MirrorCS")])]});
            var Q27;
            Q27=makeQuery(id+"F2.opExtrude","SWEPT_EDGE",EDGE,{"disambiguationData":[OSD([sQuery(id+"F1.wireOp",EDGE,"E52.MirrorCS"),sQuery(id+"F1.wireOp",EDGE,"E58.MirrorCS")])]});
            var Q28;
            Q28=makeQuery(id+"F2.opExtrude","SWEPT_EDGE",EDGE,{"disambiguationData":[OSD([sQuery(id+"F1.wireOp",EDGE,"E52.MirrorCS"),sQuery(id+"F1.wireOp",EDGE,"E60.MirrorCS")])]});
            var Q29;
            Q29=makeQuery(id+"F2.opExtrude","SWEPT_EDGE",EDGE,{"disambiguationData":[OSD([sQuery(id+"F1.wireOp",EDGE,"E52.MirrorCS"),sQuery(id+"F1.wireOp",EDGE,"E70.MirrorCS")])]});
            var Q30;
            Q30=makeQuery(id+"F2.opExtrude","SWEPT_EDGE",EDGE,{"disambiguationData":[OSD([sQuery(id+"F1.wireOp",EDGE,"E52.MirrorCS"),sQuery(id+"F1.wireOp",EDGE,"E64.MirrorCS")])]});
            var Q31;
            Q31=makeQuery(id+"F2.opExtrude","SWEPT_EDGE",EDGE,{"disambiguationData":[OSD([sQuery(id+"F1.wireOp",EDGE,"E52.MirrorCS"),sQuery(id+"F1.wireOp",EDGE,"E59.MirrorCS")])]});
            var Q32;
            Q32=makeQuery(id+"F2.opExtrude","SWEPT_EDGE",EDGE,{"disambiguationData":[OSD([sQuery(id+"F1.wireOp",EDGE,"E76.MirrorCS"),sQuery(id+"F1.wireOp",EDGE,"E84.MirrorCS")])]});
            var Q33;
            Q33=makeQuery(id+"F2.opExtrude","SWEPT_EDGE",EDGE,{"disambiguationData":[OSD([sQuery(id+"F1.wireOp",EDGE,"E76.MirrorCS"),sQuery(id+"F1.wireOp",EDGE,"E92.MirrorCS")])]});
            var Q34;
            Q34=makeQuery(id+"F2.opExtrude","SWEPT_EDGE",EDGE,{"disambiguationData":[OSD([sQuery(id+"F1.wireOp",EDGE,"E76.MirrorCS"),sQuery(id+"F1.wireOp",EDGE,"E88.MirrorCS")])]});
            var Q35;
            Q35=makeQuery(id+"F2.opExtrude","SWEPT_EDGE",EDGE,{"disambiguationData":[OSD([sQuery(id+"F1.wireOp",EDGE,"E76.MirrorCS"),sQuery(id+"F1.wireOp",EDGE,"E94.MirrorCS")])]});
            var Q36;
            Q36=makeQuery(id+"F2.opExtrude","SWEPT_EDGE",EDGE,{"disambiguationData":[OSD([sQuery(id+"F1.wireOp",EDGE,"E85.MirrorCS"),sQuery(id+"F1.wireOp",EDGE,"E93.MirrorCS")])]});
            var Q37;
            Q37=makeQuery(id+"F2.opExtrude","SWEPT_EDGE",EDGE,{"disambiguationData":[OSD([sQuery(id+"F1.wireOp",EDGE,"E87.MirrorCS"),sQuery(id+"F1.wireOp",EDGE,"E93.MirrorCS")])]});
            var Q38;
            Q38=makeQuery(id+"F2.opExtrude","SWEPT_EDGE",EDGE,{"disambiguationData":[OSD([sQuery(id+"F1.wireOp",EDGE,"E91.MirrorCS"),sQuery(id+"F1.wireOp",EDGE,"E93.MirrorCS")])]});
            var Q39;
            Q39=makeQuery(id+"F2.opExtrude","SWEPT_EDGE",EDGE,{"disambiguationData":[OSD([sQuery(id+"F1.wireOp",EDGE,"E89.MirrorCS"),sQuery(id+"F1.wireOp",EDGE,"E93.MirrorCS")])]});
            var Q40;
            Q40=makeQuery(id+"F2.opExtrude","SWEPT_EDGE",EDGE,{"disambiguationData":[OSD([sQuery(id+"F1.wireOp",EDGE,"E93.MirrorCS"),sQuery(id+"F1.wireOp",EDGE,"E94.MirrorCS")])]});
            var Q41;
            Q41=makeQuery(id+"F2.opExtrude","SWEPT_EDGE",EDGE,{"disambiguationData":[OSD([sQuery(id+"F1.wireOp",EDGE,"E88.MirrorCS"),sQuery(id+"F1.wireOp",EDGE,"E93.MirrorCS")])]});
            var Q42;
            Q42=makeQuery(id+"F2.opExtrude","SWEPT_EDGE",EDGE,{"disambiguationData":[OSD([sQuery(id+"F1.wireOp",EDGE,"E84.MirrorCS"),sQuery(id+"F1.wireOp",EDGE,"E93.MirrorCS")])]});
            var Q43;
            Q43=makeQuery(id+"F2.opExtrude","SWEPT_EDGE",EDGE,{"disambiguationData":[OSD([sQuery(id+"F1.wireOp",EDGE,"E92.MirrorCS"),sQuery(id+"F1.wireOp",EDGE,"E93.MirrorCS")])]});
            var Q44;
            Q44=makeQuery(id+"F2.opExtrude","SWEPT_EDGE",EDGE,{"disambiguationData":[OSD([sQuery(id+"F1.wireOp",EDGE,"E76.MirrorCS"),sQuery(id+"F1.wireOp",EDGE,"E85.MirrorCS")])]});
            var Q45;
            Q45=makeQuery(id+"F2.opExtrude","SWEPT_EDGE",EDGE,{"disambiguationData":[OSD([sQuery(id+"F1.wireOp",EDGE,"E76.MirrorCS"),sQuery(id+"F1.wireOp",EDGE,"E87.MirrorCS")])]});
            var Q46;
            Q46=makeQuery(id+"F2.opExtrude","SWEPT_EDGE",EDGE,{"disambiguationData":[OSD([sQuery(id+"F1.wireOp",EDGE,"E76.MirrorCS"),sQuery(id+"F1.wireOp",EDGE,"E91.MirrorCS")])]});
            var Q47;
            Q47=makeQuery(id+"F2.opExtrude","SWEPT_EDGE",EDGE,{"disambiguationData":[OSD([sQuery(id+"F1.wireOp",EDGE,"E76.MirrorCS"),sQuery(id+"F1.wireOp",EDGE,"E89.MirrorCS")])]});
            var Q48;
            Q48=makeQuery(id+"F2.opExtrude","SWEPT_EDGE",EDGE,{"disambiguationData":[OSD([sQuery(id+"F1.wireOp",EDGE,"E101.MirrorCS"),sQuery(id+"F1.wireOp",EDGE,"E116.MirrorCS")])]});
            var Q49;
            Q49=makeQuery(id+"F2.opExtrude","SWEPT_EDGE",EDGE,{"disambiguationData":[OSD([sQuery(id+"F1.wireOp",EDGE,"E101.MirrorCS"),sQuery(id+"F1.wireOp",EDGE,"E110.MirrorCS")])]});
            var Q50;
            Q50=makeQuery(id+"F2.opExtrude","SWEPT_EDGE",EDGE,{"disambiguationData":[OSD([sQuery(id+"F1.wireOp",EDGE,"E101.MirrorCS"),sQuery(id+"F1.wireOp",EDGE,"E104.MirrorCS")])]});
            var Q51;
            Q51=makeQuery(id+"F2.opExtrude","SWEPT_EDGE",EDGE,{"disambiguationData":[OSD([sQuery(id+"F1.wireOp",EDGE,"E101.MirrorCS"),sQuery(id+"F1.wireOp",EDGE,"E117.MirrorCS")])]});
            var Q52;
            Q52=makeQuery(id+"F2.opExtrude","SWEPT_EDGE",EDGE,{"disambiguationData":[OSD([sQuery(id+"F1.wireOp",EDGE,"E116.MirrorCS"),sQuery(id+"F1.wireOp",EDGE,"E118.MirrorCS")])]});
            var Q53;
            Q53=makeQuery(id+"F2.opExtrude","SWEPT_EDGE",EDGE,{"disambiguationData":[OSD([sQuery(id+"F1.wireOp",EDGE,"E110.MirrorCS"),sQuery(id+"F1.wireOp",EDGE,"E118.MirrorCS")])]});
            var Q54;
            Q54=makeQuery(id+"F2.opExtrude","SWEPT_EDGE",EDGE,{"disambiguationData":[OSD([sQuery(id+"F1.wireOp",EDGE,"E104.MirrorCS"),sQuery(id+"F1.wireOp",EDGE,"E118.MirrorCS")])]});
            var Q55;
            Q55=makeQuery(id+"F2.opExtrude","SWEPT_EDGE",EDGE,{"disambiguationData":[OSD([sQuery(id+"F1.wireOp",EDGE,"E117.MirrorCS"),sQuery(id+"F1.wireOp",EDGE,"E118.MirrorCS")])]});
            var Q56;
            Q56=makeQuery(id+"F2.opExtrude","SWEPT_EDGE",EDGE,{"disambiguationData":[OSD([sQuery(id+"F1.wireOp",EDGE,"E114.MirrorCS"),sQuery(id+"F1.wireOp",EDGE,"E118.MirrorCS")])]});
            var Q57;
            Q57=makeQuery(id+"F2.opExtrude","SWEPT_EDGE",EDGE,{"disambiguationData":[OSD([sQuery(id+"F1.wireOp",EDGE,"E107.MirrorCS"),sQuery(id+"F1.wireOp",EDGE,"E118.MirrorCS")])]});
            var Q58;
            Q58=makeQuery(id+"F2.opExtrude","SWEPT_EDGE",EDGE,{"disambiguationData":[OSD([sQuery(id+"F1.wireOp",EDGE,"E105.MirrorCS"),sQuery(id+"F1.wireOp",EDGE,"E118.MirrorCS")])]});
            var Q59;
            Q59=makeQuery(id+"F2.opExtrude","SWEPT_EDGE",EDGE,{"disambiguationData":[OSD([sQuery(id+"F1.wireOp",EDGE,"E113.MirrorCS"),sQuery(id+"F1.wireOp",EDGE,"E118.MirrorCS")])]});
            var Q60;
            Q60=makeQuery(id+"F2.opExtrude","SWEPT_EDGE",EDGE,{"disambiguationData":[OSD([sQuery(id+"F1.wireOp",EDGE,"E101.MirrorCS"),sQuery(id+"F1.wireOp",EDGE,"E114.MirrorCS")])]});
            var Q61;
            Q61=makeQuery(id+"F2.opExtrude","SWEPT_EDGE",EDGE,{"disambiguationData":[OSD([sQuery(id+"F1.wireOp",EDGE,"E101.MirrorCS"),sQuery(id+"F1.wireOp",EDGE,"E107.MirrorCS")])]});
            var Q62;
            Q62=makeQuery(id+"F2.opExtrude","SWEPT_EDGE",EDGE,{"disambiguationData":[OSD([sQuery(id+"F1.wireOp",EDGE,"E101.MirrorCS"),sQuery(id+"F1.wireOp",EDGE,"E113.MirrorCS")])]});
            var Q63;
            Q63=makeQuery(id+"F2.opExtrude","SWEPT_EDGE",EDGE,{"disambiguationData":[OSD([sQuery(id+"F1.wireOp",EDGE,"E155"),sQuery(id+"F1.wireOp",EDGE,"E156")])]});
            var Q64;
            Q64=makeQuery(id+"F2.opExtrude","SWEPT_EDGE",EDGE,{"disambiguationData":[OSD([sQuery(id+"F1.wireOp",EDGE,"E158.MirrorCS"),sQuery(id+"F1.wireOp",EDGE,"E159.MirrorCS")])]});
            var Q65;
            Q65=makeQuery(id+"F2.opExtrude","SWEPT_EDGE",EDGE,{"disambiguationData":[OSD([sQuery(id+"F1.wireOp",EDGE,"E157.MirrorCS"),sQuery(id+"F1.wireOp",EDGE,"E159.MirrorCS")])]});
            var Q66;
            Q66=makeQuery(id+"F2.opExtrude","SWEPT_EDGE",EDGE,{"disambiguationData":[OSD([sQuery(id+"F1.wireOp",EDGE,"E157.MirrorCS"),sQuery(id+"F1.wireOp",EDGE,"E158.MirrorCS")])]});
            var Q67;
            Q67=makeQuery(id+"F2.opExtrude","SWEPT_EDGE",EDGE,{"disambiguationData":[OSD([sQuery(id+"F1.wireOp",EDGE,"E154"),sQuery(id+"F1.wireOp",EDGE,"E156")])]});
            var Q68;
            Q68=makeQuery(id+"F2.opExtrude","SWEPT_EDGE",EDGE,{"disambiguationData":[OSD([sQuery(id+"F1.wireOp",EDGE,"E154"),sQuery(id+"F1.wireOp",EDGE,"E155")])]});
            var Q69;
            Q69=makeQuery(id+"F2.opExtrude","SWEPT_EDGE",EDGE,{"disambiguationData":[OSD([sQuery(id+"F1.wireOp",EDGE,"E152.MirrorCS"),sQuery(id+"F1.wireOp",EDGE,"E153.MirrorCS")])]});
            var Q70;
            Q70=makeQuery(id+"F2.opExtrude","SWEPT_EDGE",EDGE,{"disambiguationData":[OSD([sQuery(id+"F1.wireOp",EDGE,"E150.MirrorCS"),sQuery(id+"F1.wireOp",EDGE,"E152.MirrorCS")])]});
            var Q71;
            Q71=makeQuery(id+"F2.opExtrude","SWEPT_EDGE",EDGE,{"disambiguationData":[OSD([sQuery(id+"F1.wireOp",EDGE,"E151.MirrorCS"),sQuery(id+"F1.wireOp",EDGE,"E153.MirrorCS")])]});
            var Q72;
            Q72=makeQuery(id+"F2.opExtrude","SWEPT_EDGE",EDGE,{"disambiguationData":[OSD([sQuery(id+"F1.wireOp",EDGE,"E150.MirrorCS"),sQuery(id+"F1.wireOp",EDGE,"E151.MirrorCS")])]});
            var Q73;
            Q73=makeQuery(id+"F2.opExtrude","SWEPT_EDGE",EDGE,{"disambiguationData":[OSD([sQuery(id+"F1.wireOp",EDGE,"E147"),sQuery(id+"F1.wireOp",EDGE,"E148")])]});
            var Q74;
            Q74=makeQuery(id+"F2.opExtrude","SWEPT_EDGE",EDGE,{"disambiguationData":[OSD([sQuery(id+"F1.wireOp",EDGE,"E148"),sQuery(id+"F1.wireOp",EDGE,"E149")])]});
            var Q75;
            Q75=makeQuery(id+"F2.opExtrude","SWEPT_EDGE",EDGE,{"disambiguationData":[OSD([sQuery(id+"F1.wireOp",EDGE,"E146"),sQuery(id+"F1.wireOp",EDGE,"E149")])]});
            var Q76;
            Q76=makeQuery(id+"F2.opExtrude","SWEPT_EDGE",EDGE,{"disambiguationData":[OSD([sQuery(id+"F1.wireOp",EDGE,"E146"),sQuery(id+"F1.wireOp",EDGE,"E147")])]});
            var Q77;
            Q77=makeQuery(id+"F2.opExtrude","SWEPT_EDGE",EDGE,{"disambiguationData":[OSD([sQuery(id+"F1.wireOp",EDGE,"E143.MirrorCS"),sQuery(id+"F1.wireOp",EDGE,"E144.MirrorCS")])]});
            var Q78;
            Q78=makeQuery(id+"F2.opExtrude","SWEPT_EDGE",EDGE,{"disambiguationData":[OSD([sQuery(id+"F1.wireOp",EDGE,"E138"),sQuery(id+"F1.wireOp",EDGE,"E141")])]});
            var Q79;
            Q79=makeQuery(id+"F2.opExtrude","SWEPT_EDGE",EDGE,{"disambiguationData":[OSD([sQuery(id+"F1.wireOp",EDGE,"E140"),sQuery(id+"F1.wireOp",EDGE,"E141")])]});
            var Q80;
            Q80=makeQuery(id+"F2.opExtrude","SWEPT_EDGE",EDGE,{"disambiguationData":[OSD([sQuery(id+"F1.wireOp",EDGE,"E142.MirrorCS"),sQuery(id+"F1.wireOp",EDGE,"E145.MirrorCS")])]});
            var Q81;
            Q81=makeQuery(id+"F2.opExtrude","SWEPT_EDGE",EDGE,{"disambiguationData":[OSD([sQuery(id+"F1.wireOp",EDGE,"E144.MirrorCS"),sQuery(id+"F1.wireOp",EDGE,"E145.MirrorCS")])]});
            var Q82;
            Q82=makeQuery(id+"F2.opExtrude","SWEPT_EDGE",EDGE,{"disambiguationData":[OSD([sQuery(id+"F1.wireOp",EDGE,"E138"),sQuery(id+"F1.wireOp",EDGE,"E139")])]});
            var Q83;
            Q83=makeQuery(id+"F2.opExtrude","SWEPT_EDGE",EDGE,{"disambiguationData":[OSD([sQuery(id+"F1.wireOp",EDGE,"E139"),sQuery(id+"F1.wireOp",EDGE,"E140")])]});
            var Q84;
            Q84=makeQuery(id+"F2.opExtrude","SWEPT_EDGE",EDGE,{"disambiguationData":[OSD([sQuery(id+"F1.wireOp",EDGE,"E142.MirrorCS"),sQuery(id+"F1.wireOp",EDGE,"E143.MirrorCS")])]});
            var Q85;
            Q85=makeQuery(id+"F2.opExtrude","SWEPT_EDGE",EDGE,{"disambiguationData":[OSD([sQuery(id+"F1.wireOp",EDGE,"E135"),sQuery(id+"F1.wireOp",EDGE,"E137")])]});
            var Q86;
            Q86=makeQuery(id+"F2.opExtrude","SWEPT_EDGE",EDGE,{"disambiguationData":[OSD([sQuery(id+"F1.wireOp",EDGE,"E135"),sQuery(id+"F1.wireOp",EDGE,"E136")])]});
            var Q87;
            Q87=makeQuery(id+"F2.opExtrude","SWEPT_EDGE",EDGE,{"disambiguationData":[OSD([sQuery(id+"F1.wireOp",EDGE,"E136"),sQuery(id+"F1.wireOp",EDGE,"E137")])]});
            var Q88;
            Q88=makeQuery(id+"F2.opExtrude","SWEPT_EDGE",EDGE,{"disambiguationData":[OSD([sQuery(id+"F1.wireOp",EDGE,"E0.bottom"),sQuery(id+"F1.wireOp",EDGE,"E22.MirrorCS")])]});
            var Q89;
            Q89=makeQuery(id+"F2.opExtrude","SWEPT_EDGE",EDGE,{"disambiguationData":[OSD([sQuery(id+"F1.wireOp",EDGE,"E0.bottom"),sQuery(id+"F1.wireOp",EDGE,"E1")])]});
            var Q90;
            Q90=makeQuery(id+"F2.opExtrude","SWEPT_EDGE",EDGE,{"disambiguationData":[OSD([sQuery(id+"F1.wireOp",EDGE,"E1"),sQuery(id+"F1.wireOp",EDGE,"E2")])]});
            var Q91;
            Q91=makeQuery(id+"F2.opExtrude","SWEPT_EDGE",EDGE,{"disambiguationData":[OSD([sQuery(id+"F1.wireOp",EDGE,"E22.MirrorCS"),sQuery(id+"F1.wireOp",EDGE,"E23.MirrorCS")])]});
            var Q92;
            Q92=makeQuery(id+"F2.opExtrude","SWEPT_EDGE",EDGE,{"disambiguationData":[OSD([sQuery(id+"F1.wireOp",EDGE,"E23.MirrorCS"),sQuery(id+"F1.wireOp",EDGE,"E24.MirrorCS")])]});
            var Q93;
            Q93=makeQuery(id+"F2.opExtrude","SWEPT_EDGE",EDGE,{"disambiguationData":[OSD([sQuery(id+"F1.wireOp",EDGE,"E2"),sQuery(id+"F1.wireOp",EDGE,"E3")])]});
            var Q94;
            Q94=makeQuery(id+"F2.opExtrude","SWEPT_EDGE",EDGE,{"disambiguationData":[OSD([sQuery(id+"F1.wireOp",EDGE,"E160"),sQuery(id+"F1.wireOp",EDGE,"E161")])]});
            var Q95;
            Q95=makeQuery(id+"F2.opExtrude","SWEPT_EDGE",EDGE,{"disambiguationData":[OSD([sQuery(id+"F1.wireOp",EDGE,"E168.MirrorCS"),sQuery(id+"F1.wireOp",EDGE,"E169.MirrorCS")])]});
            var Q96;
            Q96=makeQuery(id+"F2.opExtrude","SWEPT_EDGE",EDGE,{"disambiguationData":[OSD([sQuery(id+"F1.wireOp",EDGE,"E0.top"),sQuery(id+"F1.wireOp",EDGE,"E168.MirrorCS")])]});
            var Q97;
            Q97=makeQuery(id+"F2.opExtrude","SWEPT_EDGE",EDGE,{"disambiguationData":[OSD([sQuery(id+"F1.wireOp",EDGE,"E0.top"),sQuery(id+"F1.wireOp",EDGE,"E160")])]});
            var Q98;
            Q98=makeQuery(id+"F2.opExtrude","SWEPT_EDGE",EDGE,{"disambiguationData":[OSD([sQuery(id+"F1.wireOp",EDGE,"E166"),sQuery(id+"F1.wireOp",EDGE,"E167")])]});
            var Q99;
            Q99=makeQuery(id+"F2.opExtrude","SWEPT_EDGE",EDGE,{"disambiguationData":[OSD([sQuery(id+"F1.wireOp",EDGE,"E173.MirrorCS"),sQuery(id+"F1.wireOp",EDGE,"E174.MirrorCS")])]});
            var Q100;
            Q100=makeQuery(id+"F2.opExtrude","SWEPT_EDGE",EDGE,{"disambiguationData":[OSD([sQuery(id+"F1.wireOp",EDGE,"E164"),sQuery(id+"F1.wireOp",EDGE,"E165")])]});
            var Q101;
            Q101=makeQuery(id+"F2.opExtrude","SWEPT_EDGE",EDGE,{"disambiguationData":[OSD([sQuery(id+"F1.wireOp",EDGE,"E165"),sQuery(id+"F1.wireOp",EDGE,"E166")])]});
            var Q102;
            Q102=makeQuery(id+"F2.opExtrude","SWEPT_EDGE",EDGE,{"disambiguationData":[OSD([sQuery(id+"F1.wireOp",EDGE,"E172.MirrorCS"),sQuery(id+"F1.wireOp",EDGE,"E173.MirrorCS")])]});
            var Q103;
            Q103=makeQuery(id+"F2.opExtrude","SWEPT_EDGE",EDGE,{"disambiguationData":[OSD([sQuery(id+"F1.wireOp",EDGE,"E171.MirrorCS"),sQuery(id+"F1.wireOp",EDGE,"E172.MirrorCS")])]});
            var Q104;
            Q104=makeQuery(id+"F2.opExtrude","SWEPT_EDGE",EDGE,{"disambiguationData":[OSD([sQuery(id+"F1.wireOp",EDGE,"E127.MirrorCS"),sQuery(id+"F1.wireOp",EDGE,"E128.MirrorCS")])]});
            var Q105;
            Q105=makeQuery(id+"F2.opExtrude","SWEPT_EDGE",EDGE,{"disambiguationData":[OSD([sQuery(id+"F1.wireOp",EDGE,"E124.top"),sQuery(id+"F1.wireOp",EDGE,"E124.right")])]});
            fillet(context, id + "F3", {"entities" : qUnion([Q0, Q1, Q2, Q3, Q4, Q5, Q6, Q7, Q8, Q9, Q10, Q11, Q12, Q13, Q14, Q15, Q16, Q17, Q18, Q19, Q20, Q21, Q22, Q23, Q24, Q25, Q26, Q27, Q28, Q29, Q30, Q31, Q32, Q33, Q34, Q35, Q36, Q37, Q38, Q39, Q40, Q41, Q42, Q43, Q44, Q45, Q46, Q47, Q48, Q49, Q50, Q51, Q52, Q53, Q54, Q55, Q56, Q57, Q58, Q59, Q60, Q61, Q62, Q63, Q64, Q65, Q66, Q67, Q68, Q69, Q70, Q71, Q72, Q73, Q74, Q75, Q76, Q77, Q78, Q79, Q80, Q81, Q82, Q83, Q84, Q85, Q86, Q87, Q88, Q89, Q90, Q91, Q92, Q93, Q94, Q95, Q96, Q97, Q98, Q99, Q100, Q101, Q102, Q103, Q104, Q105]), "radius" : 1 * mm, "tangentPropagation" : true, "allowEdgeOverflow" : false});
        }
        {
            var Q0;
            Q0=makeQuery(id+"F2.opExtrude","CAP_EDGE",EDGE,{"disambiguationData":[OSD([sQuery(id+"F1.wireOp",EDGE,"E74.MirrorC")])],"isStart":true});
            var Q1;
            Q1=makeQuery(id+"F2.opExtrude","CAP_EDGE",EDGE,{"disambiguationData":[OSD([sQuery(id+"F1.wireOp",EDGE,"E72.MirrorC")])],"isStart":true});
            var Q2;
            Q2=makeQuery(id+"F2.opExtrude","CAP_EDGE",EDGE,{"disambiguationData":[OSD([sQuery(id+"F1.wireOp",EDGE,"E71.MirrorC")])],"isStart":true});
            var Q3;
            Q3=makeQuery(id+"F2.opExtrude","CAP_EDGE",EDGE,{"disambiguationData":[OSD([sQuery(id+"F1.wireOp",EDGE,"E75.MirrorC")])],"isStart":true});
            var Q4;
            Q4=makeQuery(id+"F2.opExtrude","CAP_EDGE",EDGE,{"disambiguationData":[OSD([sQuery(id+"F1.wireOp",EDGE,"E95.MirrorC")])],"isStart":true});
            var Q5;
            Q5=makeQuery(id+"F2.opExtrude","CAP_EDGE",EDGE,{"disambiguationData":[OSD([sQuery(id+"F1.wireOp",EDGE,"E97.MirrorC")])],"isStart":true});
            var Q6;
            Q6=makeQuery(id+"F2.opExtrude","CAP_EDGE",EDGE,{"disambiguationData":[OSD([sQuery(id+"F1.wireOp",EDGE,"E98.MirrorC")])],"isStart":true});
            var Q7;
            Q7=makeQuery(id+"F2.opExtrude","CAP_EDGE",EDGE,{"disambiguationData":[OSD([sQuery(id+"F1.wireOp",EDGE,"E99.MirrorC")])],"isStart":true});
            var Q8;
            Q8=makeQuery(id+"F2.opExtrude","CAP_EDGE",EDGE,{"disambiguationData":[OSD([sQuery(id+"F1.wireOp",EDGE,"E121.MirrorC")])],"isStart":true});
            var Q9;
            Q9=makeQuery(id+"F2.opExtrude","CAP_EDGE",EDGE,{"disambiguationData":[OSD([sQuery(id+"F1.wireOp",EDGE,"E122.MirrorC")])],"isStart":true});
            var Q10;
            Q10=makeQuery(id+"F2.opExtrude","CAP_EDGE",EDGE,{"disambiguationData":[OSD([sQuery(id+"F1.wireOp",EDGE,"E120.MirrorC")])],"isStart":true});
            var Q11;
            Q11=makeQuery(id+"F2.opExtrude","CAP_EDGE",EDGE,{"disambiguationData":[OSD([sQuery(id+"F1.wireOp",EDGE,"E119.MirrorC")])],"isStart":true});
            var Q12;
            Q12=makeQuery(id+"F2.opExtrude","CAP_EDGE",EDGE,{"disambiguationData":[OSD([sQuery(id+"F1.wireOp",EDGE,"E32.MirrorC")])],"isStart":true});
            var Q13;
            Q13=makeQuery(id+"F2.opExtrude","CAP_EDGE",EDGE,{"disambiguationData":[OSD([sQuery(id+"F1.wireOp",EDGE,"E27")])],"isStart":true});
            var Q14;
            Q14=makeQuery(id+"F2.opExtrude","CAP_EDGE",EDGE,{"disambiguationData":[OSD([sQuery(id+"F1.wireOp",EDGE,"E30")])],"isStart":true});
            var Q15;
            Q15=makeQuery(id+"F2.opExtrude","CAP_EDGE",EDGE,{"disambiguationData":[OSD([sQuery(id+"F1.wireOp",EDGE,"E29.MirrorC")])],"isStart":true});
            chamfer(context, id + "F4", {"entities" : qUnion([Q0, Q1, Q2, Q3, Q4, Q5, Q6, Q7, Q8, Q9, Q10, Q11, Q12, Q13, Q14, Q15]), "width" : .5 * mm, "tangentPropagation" : true});
        }
        {
            var Q0;
            Q0=makeQuery(id+"F2.opExtrude","SWEPT_EDGE",EDGE,{"disambiguationData":[OSD([sQuery(id+"F1.wireOp",EDGE,"E6"),sQuery(id+"F1.wireOp",EDGE,"E8")])]});
            var Q1;
            Q1=makeQuery(id+"F2.opExtrude","SWEPT_EDGE",EDGE,{"disambiguationData":[OSD([sQuery(id+"F1.wireOp",EDGE,"E7"),sQuery(id+"F1.wireOp",EDGE,"E8")])]});
            var Q2;
            Q2=makeQuery(id+"F2.opExtrude","SWEPT_EDGE",EDGE,{"disambiguationData":[OSD([sQuery(id+"F1.wireOp",EDGE,"E15.MirrorCS"),sQuery(id+"F1.wireOp",EDGE,"E17.MirrorC")])]});
            var Q3;
            Q3=makeQuery(id+"F2.opExtrude","SWEPT_EDGE",EDGE,{"disambiguationData":[OSD([sQuery(id+"F1.wireOp",EDGE,"E14.MirrorCS"),sQuery(id+"F1.wireOp",EDGE,"E17.MirrorC")])]});
            var Q4;
            Q4=makeQuery(id+"F2.opExtrude","SWEPT_EDGE",EDGE,{"disambiguationData":[OSD([sQuery(id+"F1.wireOp",EDGE,"E19.MirrorCS"),sQuery(id+"F1.wireOp",EDGE,"E21.MirrorC")])]});
            var Q5;
            Q5=makeQuery(id+"F2.opExtrude","SWEPT_EDGE",EDGE,{"disambiguationData":[OSD([sQuery(id+"F1.wireOp",EDGE,"E18.MirrorCS"),sQuery(id+"F1.wireOp",EDGE,"E21.MirrorC")])]});
            var Q6;
            Q6=makeQuery(id+"F2.opExtrude","SWEPT_EDGE",EDGE,{"disambiguationData":[OSD([sQuery(id+"F1.wireOp",EDGE,"E11.MirrorC"),sQuery(id+"F1.wireOp",EDGE,"E12.MirrorCS")])]});
            var Q7;
            Q7=makeQuery(id+"F2.opExtrude","SWEPT_EDGE",EDGE,{"disambiguationData":[OSD([sQuery(id+"F1.wireOp",EDGE,"E11.MirrorC"),sQuery(id+"F1.wireOp",EDGE,"E10.MirrorCS")])]});
            fillet(context, id + "F5", {"entities" : qUnion([Q0, Q1, Q2, Q3, Q4, Q5, Q6, Q7]), "radius" : 5 * mm, "tangentPropagation" : true, "allowEdgeOverflow" : false});
        }
        {
            var Q0;
            Q0=makeQuery(id+"F2.opExtrude","CAP_FACE",FACE,{"disambiguationData":[OSD([sQuery(id+"F1.wireOp",EDGE,"E0.bottom"),sQuery(id+"F1.wireOp",EDGE,"E0.top"),sQuery(id+"F1.wireOp",EDGE,"E0.left"),sQuery(id+"F1.wireOp",EDGE,"E0.right"),sQuery(id+"F1.wireOp",EDGE,"E1"),sQuery(id+"F1.wireOp",EDGE,"E2"),sQuery(id+"F1.wireOp",EDGE,"E3"),sQuery(id+"F1.wireOp",EDGE,"E5"),sQuery(id+"F1.wireOp",EDGE,"E6"),sQuery(id+"F1.wireOp",EDGE,"E7"),sQuery(id+"F1.wireOp",EDGE,"E8"),sQuery(id+"F1.wireOp",EDGE,"E11.MirrorC"),sQuery(id+"F1.wireOp",EDGE,"E14.MirrorCS"),sQuery(id+"F1.wireOp",EDGE,"E15.MirrorCS"),sQuery(id+"F1.wireOp",EDGE,"E16.MirrorCS"),sQuery(id+"F1.wireOp",EDGE,"E17.MirrorC"),sQuery(id+"F1.wireOp",EDGE,"E18.MirrorCS"),sQuery(id+"F1.wireOp",EDGE,"E19.MirrorCS"),sQuery(id+"F1.wireOp",EDGE,"E21.MirrorC"),sQuery(id+"F1.wireOp",EDGE,"E22.MirrorCS"),sQuery(id+"F1.wireOp",EDGE,"E23.MirrorCS"),sQuery(id+"F1.wireOp",EDGE,"E24.MirrorCS"),sQuery(id+"F1.wireOp",EDGE,"E26"),sQuery(id+"F1.wireOp",EDGE,"E27"),sQuery(id+"F1.wireOp",EDGE,"E29.MirrorC"),sQuery(id+"F1.wireOp",EDGE,"E30"),sQuery(id+"F1.wireOp",EDGE,"E32.MirrorC"),sQuery(id+"F1.wireOp",EDGE,"E33"),sQuery(id+"F1.wireOp",EDGE,"E34"),sQuery(id+"F1.wireOp",EDGE,"E35"),sQuery(id+"F1.wireOp",EDGE,"E36"),sQuery(id+"F1.wireOp",EDGE,"E39"),sQuery(id+"F1.wireOp",EDGE,"E40"),sQuery(id+"F1.wireOp",EDGE,"E41"),sQuery(id+"F1.wireOp",EDGE,"E42"),sQuery(id+"F1.wireOp",EDGE,"E43"),sQuery(id+"F1.wireOp",EDGE,"E44"),sQuery(id+"F1.wireOp",EDGE,"E52.MirrorCS"),sQuery(id+"F1.wireOp",EDGE,"E58.MirrorCS"),sQuery(id+"F1.wireOp",EDGE,"E59.MirrorCS"),sQuery(id+"F1.wireOp",EDGE,"E60.MirrorCS"),sQuery(id+"F1.wireOp",EDGE,"E61.MirrorCS"),sQuery(id+"F1.wireOp",EDGE,"E64.MirrorCS"),sQuery(id+"F1.wireOp",EDGE,"E65.MirrorCS"),sQuery(id+"F1.wireOp",EDGE,"E66.MirrorCS"),sQuery(id+"F1.wireOp",EDGE,"E68.MirrorCS"),sQuery(id+"F1.wireOp",EDGE,"E70.MirrorCS"),sQuery(id+"F1.wireOp",EDGE,"E71.MirrorC"),sQuery(id+"F1.wireOp",EDGE,"E72.MirrorC"),sQuery(id+"F1.wireOp",EDGE,"E73.MirrorC"),sQuery(id+"F1.wireOp",EDGE,"E74.MirrorC"),sQuery(id+"F1.wireOp",EDGE,"E75.MirrorC"),sQuery(id+"F1.wireOp",EDGE,"E76.MirrorCS"),sQuery(id+"F1.wireOp",EDGE,"E84.MirrorCS"),sQuery(id+"F1.wireOp",EDGE,"E85.MirrorCS"),sQuery(id+"F1.wireOp",EDGE,"E87.MirrorCS"),sQuery(id+"F1.wireOp",EDGE,"E88.MirrorCS"),sQuery(id+"F1.wireOp",EDGE,"E89.MirrorCS"),sQuery(id+"F1.wireOp",EDGE,"E91.MirrorCS"),sQuery(id+"F1.wireOp",EDGE,"E92.MirrorCS"),sQuery(id+"F1.wireOp",EDGE,"E93.MirrorCS"),sQuery(id+"F1.wireOp",EDGE,"E94.MirrorCS"),sQuery(id+"F1.wireOp",EDGE,"E95.MirrorC"),sQuery(id+"F1.wireOp",EDGE,"E96.MirrorC"),sQuery(id+"F1.wireOp",EDGE,"E97.MirrorC"),sQuery(id+"F1.wireOp",EDGE,"E98.MirrorC"),sQuery(id+"F1.wireOp",EDGE,"E99.MirrorC"),sQuery(id+"F1.wireOp",EDGE,"E101.MirrorCS"),sQuery(id+"F1.wireOp",EDGE,"E104.MirrorCS"),sQuery(id+"F1.wireOp",EDGE,"E105.MirrorCS"),sQuery(id+"F1.wireOp",EDGE,"E107.MirrorCS"),sQuery(id+"F1.wireOp",EDGE,"E110.MirrorCS"),sQuery(id+"F1.wireOp",EDGE,"E12.MirrorCS"),sQuery(id+"F1.wireOp",EDGE,"E113.MirrorCS"),sQuery(id+"F1.wireOp",EDGE,"E114.MirrorCS"),sQuery(id+"F1.wireOp",EDGE,"E10.MirrorCS"),sQuery(id+"F1.wireOp",EDGE,"E116.MirrorCS"),sQuery(id+"F1.wireOp",EDGE,"E117.MirrorCS"),sQuery(id+"F1.wireOp",EDGE,"E118.MirrorCS"),sQuery(id+"F1.wireOp",EDGE,"E119.MirrorC"),sQuery(id+"F1.wireOp",EDGE,"E120.MirrorC"),sQuery(id+"F1.wireOp",EDGE,"E121.MirrorC"),sQuery(id+"F1.wireOp",EDGE,"E122.MirrorC"),sQuery(id+"F1.wireOp",EDGE,"E123.MirrorC"),sQuery(id+"F1.wireOp",EDGE,"E124.bottom"),sQuery(id+"F1.wireOp",EDGE,"E124.top"),sQuery(id+"F1.wireOp",EDGE,"E124.left"),sQuery(id+"F1.wireOp",EDGE,"E124.right"),sQuery(id+"F1.wireOp",EDGE,"E125.MirrorCS"),sQuery(id+"F1.wireOp",EDGE,"E126.MirrorCS"),sQuery(id+"F1.wireOp",EDGE,"E127.MirrorCS"),sQuery(id+"F1.wireOp",EDGE,"E128.MirrorCS"),sQuery(id+"F1.wireOp",EDGE,"E129.bottom"),sQuery(id+"F1.wireOp",EDGE,"E129.top"),sQuery(id+"F1.wireOp",EDGE,"E129.left"),sQuery(id+"F1.wireOp",EDGE,"E129.right"),sQuery(id+"F1.wireOp",EDGE,"E130.MirrorCS"),sQuery(id+"F1.wireOp",EDGE,"E131.MirrorCS"),sQuery(id+"F1.wireOp",EDGE,"E132.MirrorCS"),sQuery(id+"F1.wireOp",EDGE,"E133.MirrorCS"),sQuery(id+"F1.wireOp",EDGE,"E134.bottom"),sQuery(id+"F1.wireOp",EDGE,"E134.top"),sQuery(id+"F1.wireOp",EDGE,"E134.left"),sQuery(id+"F1.wireOp",EDGE,"E134.right"),sQuery(id+"F1.wireOp",EDGE,"E135"),sQuery(id+"F1.wireOp",EDGE,"E136"),sQuery(id+"F1.wireOp",EDGE,"E137"),sQuery(id+"F1.wireOp",EDGE,"E138"),sQuery(id+"F1.wireOp",EDGE,"E139"),sQuery(id+"F1.wireOp",EDGE,"E140"),sQuery(id+"F1.wireOp",EDGE,"E141"),sQuery(id+"F1.wireOp",EDGE,"E142.MirrorCS"),sQuery(id+"F1.wireOp",EDGE,"E143.MirrorCS"),sQuery(id+"F1.wireOp",EDGE,"E144.MirrorCS"),sQuery(id+"F1.wireOp",EDGE,"E145.MirrorCS"),sQuery(id+"F1.wireOp",EDGE,"E146"),sQuery(id+"F1.wireOp",EDGE,"E147"),sQuery(id+"F1.wireOp",EDGE,"E148"),sQuery(id+"F1.wireOp",EDGE,"E149"),sQuery(id+"F1.wireOp",EDGE,"E150.MirrorCS"),sQuery(id+"F1.wireOp",EDGE,"E151.MirrorCS"),sQuery(id+"F1.wireOp",EDGE,"E152.MirrorCS"),sQuery(id+"F1.wireOp",EDGE,"E153.MirrorCS"),sQuery(id+"F1.wireOp",EDGE,"E154"),sQuery(id+"F1.wireOp",EDGE,"E155"),sQuery(id+"F1.wireOp",EDGE,"E156"),sQuery(id+"F1.wireOp",EDGE,"E157.MirrorCS"),sQuery(id+"F1.wireOp",EDGE,"E158.MirrorCS"),sQuery(id+"F1.wireOp",EDGE,"E159.MirrorCS"),sQuery(id+"F1.wireOp",EDGE,"E160"),sQuery(id+"F1.wireOp",EDGE,"E161"),sQuery(id+"F1.wireOp",EDGE,"E162"),sQuery(id+"F1.wireOp",EDGE,"E163"),sQuery(id+"F1.wireOp",EDGE,"E164"),sQuery(id+"F1.wireOp",EDGE,"E165"),sQuery(id+"F1.wireOp",EDGE,"E166"),sQuery(id+"F1.wireOp",EDGE,"E167"),sQuery(id+"F1.wireOp",EDGE,"E168.MirrorCS"),sQuery(id+"F1.wireOp",EDGE,"E169.MirrorCS"),sQuery(id+"F1.wireOp",EDGE,"E170.MirrorCS"),sQuery(id+"F1.wireOp",EDGE,"E171.MirrorCS"),sQuery(id+"F1.wireOp",EDGE,"E172.MirrorCS"),sQuery(id+"F1.wireOp",EDGE,"E173.MirrorCS"),sQuery(id+"F1.wireOp",EDGE,"E174.MirrorCS"),sQuery(id+"F1.wireOp",EDGE,"E175.MirrorCS")])],"isStart":false});
            var Q1;
            Q1=makeQuery(id+"F2.opExtrude","CAP_FACE",FACE,{"disambiguationData":[OSD([sQuery(id+"F1.wireOp",EDGE,"E0.bottom"),sQuery(id+"F1.wireOp",EDGE,"E0.top"),sQuery(id+"F1.wireOp",EDGE,"E0.left"),sQuery(id+"F1.wireOp",EDGE,"E0.right"),sQuery(id+"F1.wireOp",EDGE,"E1"),sQuery(id+"F1.wireOp",EDGE,"E2"),sQuery(id+"F1.wireOp",EDGE,"E3"),sQuery(id+"F1.wireOp",EDGE,"E5"),sQuery(id+"F1.wireOp",EDGE,"E6"),sQuery(id+"F1.wireOp",EDGE,"E7"),sQuery(id+"F1.wireOp",EDGE,"E8"),sQuery(id+"F1.wireOp",EDGE,"E11.MirrorC"),sQuery(id+"F1.wireOp",EDGE,"E14.MirrorCS"),sQuery(id+"F1.wireOp",EDGE,"E15.MirrorCS"),sQuery(id+"F1.wireOp",EDGE,"E16.MirrorCS"),sQuery(id+"F1.wireOp",EDGE,"E17.MirrorC"),sQuery(id+"F1.wireOp",EDGE,"E18.MirrorCS"),sQuery(id+"F1.wireOp",EDGE,"E19.MirrorCS"),sQuery(id+"F1.wireOp",EDGE,"E21.MirrorC"),sQuery(id+"F1.wireOp",EDGE,"E22.MirrorCS"),sQuery(id+"F1.wireOp",EDGE,"E23.MirrorCS"),sQuery(id+"F1.wireOp",EDGE,"E24.MirrorCS"),sQuery(id+"F1.wireOp",EDGE,"E26"),sQuery(id+"F1.wireOp",EDGE,"E27"),sQuery(id+"F1.wireOp",EDGE,"E29.MirrorC"),sQuery(id+"F1.wireOp",EDGE,"E30"),sQuery(id+"F1.wireOp",EDGE,"E32.MirrorC"),sQuery(id+"F1.wireOp",EDGE,"E33"),sQuery(id+"F1.wireOp",EDGE,"E34"),sQuery(id+"F1.wireOp",EDGE,"E35"),sQuery(id+"F1.wireOp",EDGE,"E36"),sQuery(id+"F1.wireOp",EDGE,"E39"),sQuery(id+"F1.wireOp",EDGE,"E40"),sQuery(id+"F1.wireOp",EDGE,"E41"),sQuery(id+"F1.wireOp",EDGE,"E42"),sQuery(id+"F1.wireOp",EDGE,"E43"),sQuery(id+"F1.wireOp",EDGE,"E44"),sQuery(id+"F1.wireOp",EDGE,"E52.MirrorCS"),sQuery(id+"F1.wireOp",EDGE,"E58.MirrorCS"),sQuery(id+"F1.wireOp",EDGE,"E59.MirrorCS"),sQuery(id+"F1.wireOp",EDGE,"E60.MirrorCS"),sQuery(id+"F1.wireOp",EDGE,"E61.MirrorCS"),sQuery(id+"F1.wireOp",EDGE,"E64.MirrorCS"),sQuery(id+"F1.wireOp",EDGE,"E65.MirrorCS"),sQuery(id+"F1.wireOp",EDGE,"E66.MirrorCS"),sQuery(id+"F1.wireOp",EDGE,"E68.MirrorCS"),sQuery(id+"F1.wireOp",EDGE,"E70.MirrorCS"),sQuery(id+"F1.wireOp",EDGE,"E71.MirrorC"),sQuery(id+"F1.wireOp",EDGE,"E72.MirrorC"),sQuery(id+"F1.wireOp",EDGE,"E73.MirrorC"),sQuery(id+"F1.wireOp",EDGE,"E74.MirrorC"),sQuery(id+"F1.wireOp",EDGE,"E75.MirrorC"),sQuery(id+"F1.wireOp",EDGE,"E76.MirrorCS"),sQuery(id+"F1.wireOp",EDGE,"E84.MirrorCS"),sQuery(id+"F1.wireOp",EDGE,"E85.MirrorCS"),sQuery(id+"F1.wireOp",EDGE,"E87.MirrorCS"),sQuery(id+"F1.wireOp",EDGE,"E88.MirrorCS"),sQuery(id+"F1.wireOp",EDGE,"E89.MirrorCS"),sQuery(id+"F1.wireOp",EDGE,"E91.MirrorCS"),sQuery(id+"F1.wireOp",EDGE,"E92.MirrorCS"),sQuery(id+"F1.wireOp",EDGE,"E93.MirrorCS"),sQuery(id+"F1.wireOp",EDGE,"E94.MirrorCS"),sQuery(id+"F1.wireOp",EDGE,"E95.MirrorC"),sQuery(id+"F1.wireOp",EDGE,"E96.MirrorC"),sQuery(id+"F1.wireOp",EDGE,"E97.MirrorC"),sQuery(id+"F1.wireOp",EDGE,"E98.MirrorC"),sQuery(id+"F1.wireOp",EDGE,"E99.MirrorC"),sQuery(id+"F1.wireOp",EDGE,"E101.MirrorCS"),sQuery(id+"F1.wireOp",EDGE,"E104.MirrorCS"),sQuery(id+"F1.wireOp",EDGE,"E105.MirrorCS"),sQuery(id+"F1.wireOp",EDGE,"E107.MirrorCS"),sQuery(id+"F1.wireOp",EDGE,"E110.MirrorCS"),sQuery(id+"F1.wireOp",EDGE,"E12.MirrorCS"),sQuery(id+"F1.wireOp",EDGE,"E113.MirrorCS"),sQuery(id+"F1.wireOp",EDGE,"E114.MirrorCS"),sQuery(id+"F1.wireOp",EDGE,"E10.MirrorCS"),sQuery(id+"F1.wireOp",EDGE,"E116.MirrorCS"),sQuery(id+"F1.wireOp",EDGE,"E117.MirrorCS"),sQuery(id+"F1.wireOp",EDGE,"E118.MirrorCS"),sQuery(id+"F1.wireOp",EDGE,"E119.MirrorC"),sQuery(id+"F1.wireOp",EDGE,"E120.MirrorC"),sQuery(id+"F1.wireOp",EDGE,"E121.MirrorC"),sQuery(id+"F1.wireOp",EDGE,"E122.MirrorC"),sQuery(id+"F1.wireOp",EDGE,"E123.MirrorC"),sQuery(id+"F1.wireOp",EDGE,"E124.bottom"),sQuery(id+"F1.wireOp",EDGE,"E124.top"),sQuery(id+"F1.wireOp",EDGE,"E124.left"),sQuery(id+"F1.wireOp",EDGE,"E124.right"),sQuery(id+"F1.wireOp",EDGE,"E125.MirrorCS"),sQuery(id+"F1.wireOp",EDGE,"E126.MirrorCS"),sQuery(id+"F1.wireOp",EDGE,"E127.MirrorCS"),sQuery(id+"F1.wireOp",EDGE,"E128.MirrorCS"),sQuery(id+"F1.wireOp",EDGE,"E129.bottom"),sQuery(id+"F1.wireOp",EDGE,"E129.top"),sQuery(id+"F1.wireOp",EDGE,"E129.left"),sQuery(id+"F1.wireOp",EDGE,"E129.right"),sQuery(id+"F1.wireOp",EDGE,"E130.MirrorCS"),sQuery(id+"F1.wireOp",EDGE,"E131.MirrorCS"),sQuery(id+"F1.wireOp",EDGE,"E132.MirrorCS"),sQuery(id+"F1.wireOp",EDGE,"E133.MirrorCS"),sQuery(id+"F1.wireOp",EDGE,"E134.bottom"),sQuery(id+"F1.wireOp",EDGE,"E134.top"),sQuery(id+"F1.wireOp",EDGE,"E134.left"),sQuery(id+"F1.wireOp",EDGE,"E134.right"),sQuery(id+"F1.wireOp",EDGE,"E135"),sQuery(id+"F1.wireOp",EDGE,"E136"),sQuery(id+"F1.wireOp",EDGE,"E137"),sQuery(id+"F1.wireOp",EDGE,"E138"),sQuery(id+"F1.wireOp",EDGE,"E139"),sQuery(id+"F1.wireOp",EDGE,"E140"),sQuery(id+"F1.wireOp",EDGE,"E141"),sQuery(id+"F1.wireOp",EDGE,"E142.MirrorCS"),sQuery(id+"F1.wireOp",EDGE,"E143.MirrorCS"),sQuery(id+"F1.wireOp",EDGE,"E144.MirrorCS"),sQuery(id+"F1.wireOp",EDGE,"E145.MirrorCS"),sQuery(id+"F1.wireOp",EDGE,"E146"),sQuery(id+"F1.wireOp",EDGE,"E147"),sQuery(id+"F1.wireOp",EDGE,"E148"),sQuery(id+"F1.wireOp",EDGE,"E149"),sQuery(id+"F1.wireOp",EDGE,"E150.MirrorCS"),sQuery(id+"F1.wireOp",EDGE,"E151.MirrorCS"),sQuery(id+"F1.wireOp",EDGE,"E152.MirrorCS"),sQuery(id+"F1.wireOp",EDGE,"E153.MirrorCS"),sQuery(id+"F1.wireOp",EDGE,"E154"),sQuery(id+"F1.wireOp",EDGE,"E155"),sQuery(id+"F1.wireOp",EDGE,"E156"),sQuery(id+"F1.wireOp",EDGE,"E157.MirrorCS"),sQuery(id+"F1.wireOp",EDGE,"E158.MirrorCS"),sQuery(id+"F1.wireOp",EDGE,"E159.MirrorCS"),sQuery(id+"F1.wireOp",EDGE,"E160"),sQuery(id+"F1.wireOp",EDGE,"E161"),sQuery(id+"F1.wireOp",EDGE,"E162"),sQuery(id+"F1.wireOp",EDGE,"E163"),sQuery(id+"F1.wireOp",EDGE,"E164"),sQuery(id+"F1.wireOp",EDGE,"E165"),sQuery(id+"F1.wireOp",EDGE,"E166"),sQuery(id+"F1.wireOp",EDGE,"E167"),sQuery(id+"F1.wireOp",EDGE,"E168.MirrorCS"),sQuery(id+"F1.wireOp",EDGE,"E169.MirrorCS"),sQuery(id+"F1.wireOp",EDGE,"E170.MirrorCS"),sQuery(id+"F1.wireOp",EDGE,"E171.MirrorCS"),sQuery(id+"F1.wireOp",EDGE,"E172.MirrorCS"),sQuery(id+"F1.wireOp",EDGE,"E173.MirrorCS"),sQuery(id+"F1.wireOp",EDGE,"E174.MirrorCS"),sQuery(id+"F1.wireOp",EDGE,"E175.MirrorCS")])],"isStart":true});
            fillet(context, id + "F6", {"entities" : qUnion([Q0, Q1]), "radius" : .5 * mm, "tangentPropagation" : true, "allowEdgeOverflow" : false});
        }
    });
